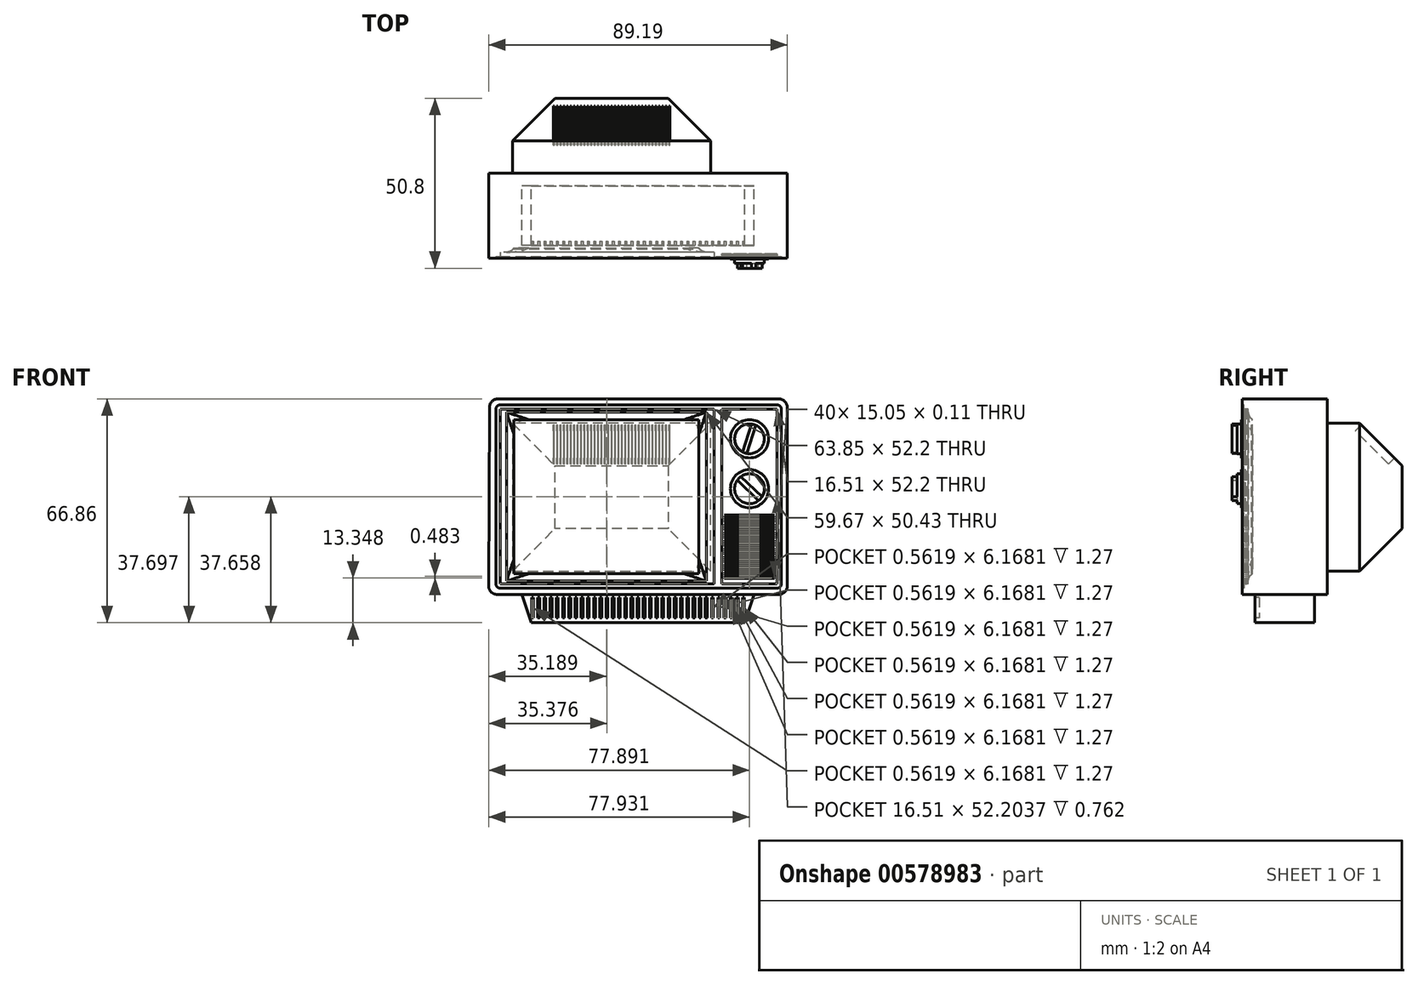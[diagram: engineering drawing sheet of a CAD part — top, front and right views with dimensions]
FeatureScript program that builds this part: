
annotation { "Feature Type Name" : "Feature", "Feature Type Description" : "" }
export const myFeature = defineFeature(function(context is Context, id is Id, definition is map)
    precondition{}
    {
        {
            var Q0;
            Q0=qCreatedBy(makeId("Front.planeOp"),FACE);
            var sketch = newSketch(context, id + "F0", { "sketchPlane" : qUnion([Q0])});
            skLineSegment(sketch, "E0", {"start": v(-47.46, 45.8) * mm, "end": v(41.44, 45.8) * mm});
            skLineSegment(sketch, "E1", {"start": v(41.44, 45.8) * mm, "end": v(41.44, -12.62) * mm});
            skLineSegment(sketch, "E2", {"start": v(41.44, -12.62) * mm, "end": v(-47.76, -12.62) * mm});
            skLineSegment(sketch, "E3", {"start": v(-47.76, -12.62) * mm, "end": v(-47.46, 45.8) * mm});
            skLineSegment(sketch, "E4", {"start": v(-35.06, -12.62) * mm, "end": v(-35.06, -21.06) * mm});
            skLineSegment(sketch, "E5", {"start": v(-35.06, -21.06) * mm, "end": v(28.74, -21.06) * mm});
            skLineSegment(sketch, "E6", {"start": v(28.74, -21.06) * mm, "end": v(28.74, -12.62) * mm});
            skLineSegment(sketch, "E7", {"start": v(-35.06, -21.06) * mm, "end": v(-37.87, -12.62) * mm});
            skLineSegment(sketch, "E8", {"start": v(28.74, -21.06) * mm, "end": v(31.55, -12.62) * mm});
            skSolve(sketch);
        }
        {
            var Q0;
            Q0=makeQuery(id+"F0.imprint","IMPRINT",FACE,{"disambiguationData":[TD([[makeQuery(id+"F0.imprint","IMPRINT",EDGE,{"derivedFrom":sQuery(id+"F0.wireOp",EDGE,"E0")}),-1.0]])]});
            extrude(context, id + "F1", {"entities" : qUnion([Q0]), "endBound" : BoundingType.SYMMETRIC, "depth" : 25.4 * mm, "offsetDistance" : 25.4 * mm});
        }
        {
            var Q0;
            {var subQ0=sQuery(id+"F0.wireOp",EDGE,"E4");Q0=makeQuery(id+"F0.imprint","IMPRINT",FACE,{"disambiguationData":[TD([[makeQuery(id+"F0.imprint","IMPRINT",EDGE,{"derivedFrom":subQ0}),1.0]])]});}
            var Q1;
            {var subQ0=sQuery(id+"F0.wireOp",EDGE,"E4");Q1=makeQuery(id+"F0.imprint","IMPRINT",FACE,{"disambiguationData":[TD([[makeQuery(id+"F0.imprint","IMPRINT",EDGE,{"derivedFrom":subQ0}),-1.0]])]});}
            var Q2;
            {var subQ0=sQuery(id+"F0.wireOp",EDGE,"E6");Q2=makeQuery(id+"F0.imprint","IMPRINT",FACE,{"disambiguationData":[TD([[makeQuery(id+"F0.imprint","IMPRINT",EDGE,{"derivedFrom":subQ0}),-1.0]])]});}
            extrude(context, id + "F2", {"entities" : qUnion([Q0, Q1, Q2]), "endBound" : BoundingType.SYMMETRIC, "depth" : 17.78 * mm, "offsetDistance" : 25.4 * mm});
        }
        {
            var Q0;
            Q0=makeQuery(id+"F1.opExtrude","CAP_FACE",FACE,{"disambiguationData":[OSD([sQuery(id+"F0.wireOp",EDGE,"E0"),sQuery(id+"F0.wireOp",EDGE,"E1"),sQuery(id+"F0.wireOp",EDGE,"E2"),sQuery(id+"F0.wireOp",EDGE,"E3")])],"isStart":false});
            var sketch = newSketch(context, id + "F3", { "sketchPlane" : qUnion([Q0])});
            skLineSegment(sketch, "E9", {"start": v(39.7, -10.73) * mm, "end": v(39.7, 44) * mm});
            skLineSegment(sketch, "E10", {"start": v(39.7, 44) * mm, "end": v(-45.57, 44) * mm});
            skLineSegment(sketch, "E11", {"start": v(-45.57, 44) * mm, "end": v(-45.57, -10.73) * mm});
            skLineSegment(sketch, "E12", {"start": v(-45.57, -10.73) * mm, "end": v(39.7, -10.73) * mm});
            skSolve(sketch);
        }
        {
            var Q0;
            Q0=makeQuery(id+"F1.opExtrude","SWEPT_EDGE",EDGE,{"disambiguationData":[OSD([sQuery(id+"F0.wireOp",EDGE,"E2"),sQuery(id+"F0.wireOp",EDGE,"E3")])]});
            var Q1;
            Q1=makeQuery(id+"F1.opExtrude","SWEPT_EDGE",EDGE,{"disambiguationData":[OSD([sQuery(id+"F0.wireOp",EDGE,"E1"),sQuery(id+"F0.wireOp",EDGE,"E2")])]});
            var Q2;
            Q2=makeQuery(id+"F1.opExtrude","SWEPT_EDGE",EDGE,{"disambiguationData":[OSD([sQuery(id+"F0.wireOp",EDGE,"E0"),sQuery(id+"F0.wireOp",EDGE,"E1")])]});
            var Q3;
            Q3=makeQuery(id+"F1.opExtrude","SWEPT_EDGE",EDGE,{"disambiguationData":[OSD([sQuery(id+"F0.wireOp",EDGE,"E0"),sQuery(id+"F0.wireOp",EDGE,"E3")])]});
            fillet(context, id + "F4", {"entities" : qUnion([Q0, Q1, Q2, Q3]), "radius" : 2.54 * mm, "tangentPropagation" : true, "allowEdgeOverflow" : false});
        }
        {
            var Q0;
            Q0 = qSketchRegion(id + "F3", true);
            extrude(context, id + "F5", {"entities" : qUnion([Q0]), "operationType" : NewBodyOperationType.REMOVE, "oppositeDirection" : true, "depth" : 0.5 * mm, "offsetDistance" : 25.4 * mm});
        }
        {
            var Q0;
            Q0=makeQuery(id+"F5.boolean.opBoolean","COPY",EDGE,{"derivedFrom":makeQuery(id+"F5.opExtrude","SWEPT_EDGE",EDGE,{"disambiguationData":[OSD([sQuery(id+"F3.wireOp",EDGE,"E10"),sQuery(id+"F3.wireOp",EDGE,"E11")])]})});
            var Q1;
            Q1=makeQuery(id+"F5.boolean.opBoolean","COPY",EDGE,{"derivedFrom":makeQuery(id+"F5.opExtrude","SWEPT_EDGE",EDGE,{"disambiguationData":[OSD([sQuery(id+"F3.wireOp",EDGE,"E9"),sQuery(id+"F3.wireOp",EDGE,"E10")])]})});
            var Q2;
            Q2=makeQuery(id+"F5.boolean.opBoolean","COPY",EDGE,{"derivedFrom":makeQuery(id+"F5.opExtrude","SWEPT_EDGE",EDGE,{"disambiguationData":[OSD([sQuery(id+"F3.wireOp",EDGE,"E9"),sQuery(id+"F3.wireOp",EDGE,"E12")])]})});
            var Q3;
            Q3=makeQuery(id+"F5.boolean.opBoolean","COPY",EDGE,{"derivedFrom":makeQuery(id+"F5.opExtrude","SWEPT_EDGE",EDGE,{"disambiguationData":[OSD([sQuery(id+"F3.wireOp",EDGE,"E11"),sQuery(id+"F3.wireOp",EDGE,"E12")])]})});
            fillet(context, id + "F6", {"entities" : qUnion([Q0, Q1, Q2, Q3]), "radius" : 1.27 * mm, "tangentPropagation" : true, "allowEdgeOverflow" : false});
        }
        {
            var Q0;
            Q0=makeQuery(id+"F1.opExtrude","CAP_FACE",FACE,{"disambiguationData":[OSD([sQuery(id+"F0.wireOp",EDGE,"E0"),sQuery(id+"F0.wireOp",EDGE,"E1"),sQuery(id+"F0.wireOp",EDGE,"E2"),sQuery(id+"F0.wireOp",EDGE,"E3")])],"isStart":true});
            var sketch = newSketch(context, id + "F7", { "sketchPlane" : qUnion([Q0])});
            skSolve(sketch);
        }
        {
            var Q0;
            Q0=makeQuery(id+"F5.boolean.opBoolean","COPY",FACE,{"derivedFrom":makeQuery(id+"F5.opExtrude","CAP_FACE",FACE,{"disambiguationData":[OSD([sQuery(id+"F3.wireOp",EDGE,"E9"),sQuery(id+"F3.wireOp",EDGE,"E10"),sQuery(id+"F3.wireOp",EDGE,"E11"),sQuery(id+"F3.wireOp",EDGE,"E12")])],"isStart":false})});
            var sketch = newSketch(context, id + "F8", { "sketchPlane" : qUnion([Q0])});
            skLineSegment(sketch, "E13", {"start": v(38.44, 42.74) * mm, "end": v(38.44, -9.46) * mm});
            skLineSegment(sketch, "E14", {"start": v(38.44, -9.46) * mm, "end": v(21.93, -9.46) * mm});
            skLineSegment(sketch, "E15", {"start": v(21.93, -9.46) * mm, "end": v(21.93, 42.74) * mm});
            skLineSegment(sketch, "E16", {"start": v(21.93, 42.74) * mm, "end": v(38.44, 42.74) * mm});
            skLineSegment(sketch, "E17", {"start": v(19.55, 42.74) * mm, "end": v(-44.3, 42.74) * mm});
            skLineSegment(sketch, "E18", {"start": v(-44.3, 42.74) * mm, "end": v(-44.3, -9.46) * mm});
            skLineSegment(sketch, "E19", {"start": v(-44.3, -9.46) * mm, "end": v(19.55, -9.46) * mm});
            skLineSegment(sketch, "E20", {"start": v(19.55, -9.46) * mm, "end": v(19.55, 42.74) * mm});
            skSolve(sketch);
        }
        {
            var Q0;
            {var subQ3=sQuery(id+"F0.wireOp",EDGE,"E0");Q0=makeQuery(id+"F7.imprint","IMPRINT",FACE,{"disambiguationData":[TD([[makeQuery(id+"F7.imprint","IMPRINT",EDGE,{"derivedFrom":makeQuery(id+"F1.opExtrude","CAP_EDGE",EDGE,{"disambiguationData":[OSD([subQ3])],"isStart":true})}),1.0]])]});}
            var sketch = newSketch(context, id + "F9", { "sketchPlane" : qUnion([Q0])});
            skLineSegment(sketch, "E21.bottom", {"start": v(-18.58, 38.52) * mm, "end": v(40.61, 38.52) * mm});
            skLineSegment(sketch, "E21.top", {"start": v(-18.58, -5.65) * mm, "end": v(40.61, -5.65) * mm});
            skLineSegment(sketch, "E21.left", {"start": v(-18.58, 38.52) * mm, "end": v(-18.58, -5.65) * mm});
            skLineSegment(sketch, "E21.right", {"start": v(40.61, 38.52) * mm, "end": v(40.61, -5.65) * mm});
            skSolve(sketch);
        }
        {
            var Q0;
            Q0 = qSketchRegion(id + "F9", true);
            extrude(context, id + "F10", {"entities" : qUnion([Q0]), "depth" : 22.35 * mm, "offsetDistance" : 25.4 * mm});
        }
        {
            var Q0;
            Q0=makeQuery(id+"F10.opExtrude","CAP_EDGE",EDGE,{"disambiguationData":[OSD([sQuery(id+"F9.wireOp",EDGE,"E21.left")])],"isStart":false});
            var Q1;
            Q1=makeQuery(id+"F10.opExtrude","CAP_EDGE",EDGE,{"disambiguationData":[OSD([sQuery(id+"F9.wireOp",EDGE,"E21.bottom")])],"isStart":false});
            var Q2;
            Q2=makeQuery(id+"F10.opExtrude","CAP_EDGE",EDGE,{"disambiguationData":[OSD([sQuery(id+"F9.wireOp",EDGE,"E21.right")])],"isStart":false});
            var Q3;
            Q3=makeQuery(id+"F10.opExtrude","CAP_EDGE",EDGE,{"disambiguationData":[OSD([sQuery(id+"F9.wireOp",EDGE,"E21.top")])],"isStart":false});
            chamfer(context, id + "F11", {"entities" : qUnion([Q0, Q1, Q2, Q3]), "width" : 12.7 * mm, "tangentPropagation" : true});
        }
        {
            var Q0;
            Q0=makeQuery(id+"F8.imprint","IMPRINT",FACE,{"disambiguationData":[TD([[makeQuery(id+"F8.imprint","IMPRINT",EDGE,{"derivedFrom":sQuery(id+"F8.wireOp",EDGE,"E17")}),1.0]])]});
            var sketch = newSketch(context, id + "F12", { "sketchPlane" : qUnion([Q0])});
            skLineSegment(sketch, "E22", {"start": v(-40.2, 39.61) * mm, "end": v(15.07, 39.61) * mm});
            skLineSegment(sketch, "E23", {"start": v(15.07, 39.61) * mm, "end": v(15.07, -6.42) * mm});
            skLineSegment(sketch, "E24", {"start": v(15.07, -6.42) * mm, "end": v(-40.2, -6.42) * mm});
            skLineSegment(sketch, "E25", {"start": v(-40.2, -6.42) * mm, "end": v(-40.2, 39.61) * mm});
            skSolve(sketch);
        }
        {
            var Q0;
            Q0=makeQuery(id+"F12.imprint","IMPRINT",FACE,{"disambiguationData":[TD([[makeQuery(id+"F12.imprint","IMPRINT",EDGE,{"derivedFrom":sQuery(id+"F12.wireOp",EDGE,"E22")}),-1.0]])]});
            extrude(context, id + "F13", {"entities" : qUnion([Q0]), "operationType" : NewBodyOperationType.REMOVE, "oppositeDirection" : true, "depth" : 2.54 * mm, "offsetDistance" : 25.4 * mm});
        }
        {
            var Q0;
            Q0=makeQuery(id+"F8.imprint","IMPRINT",FACE,{"disambiguationData":[TD([[makeQuery(id+"F8.imprint","IMPRINT",EDGE,{"derivedFrom":sQuery(id+"F8.wireOp",EDGE,"E17")}),1.0]])]});
            extrude(context, id + "F14", {"entities" : qUnion([Q0]), "operationType" : NewBodyOperationType.REMOVE, "oppositeDirection" : true, "depth" : 1.27 * mm, "offsetDistance" : 25.4 * mm});
        }
        {
            var Q0;
            Q0=makeQuery(id+"F14.boolean.opBoolean","INTERSECT",EDGE,{"derivedFrom":[makeQuery(id+"F13.boolean.opBoolean","COPY",FACE,{"derivedFrom":makeQuery(id+"F13.opExtrude","SWEPT_FACE",FACE,{"disambiguationData":[OSD([sQuery(id+"F12.wireOp",EDGE,"E25")])]})}),makeQuery(id+"F14.opExtrude","CAP_FACE",FACE,{"disambiguationData":[OSD([sQuery(id+"F8.wireOp",EDGE,"E17"),sQuery(id+"F8.wireOp",EDGE,"E18"),sQuery(id+"F8.wireOp",EDGE,"E19"),sQuery(id+"F8.wireOp",EDGE,"E20")])],"isStart":false})]});
            var Q1;
            Q1=makeQuery(id+"F14.boolean.opBoolean","INTERSECT",EDGE,{"derivedFrom":[makeQuery(id+"F13.boolean.opBoolean","COPY",FACE,{"derivedFrom":makeQuery(id+"F13.opExtrude","SWEPT_FACE",FACE,{"disambiguationData":[OSD([sQuery(id+"F12.wireOp",EDGE,"E22")])]})}),makeQuery(id+"F14.opExtrude","CAP_FACE",FACE,{"disambiguationData":[OSD([sQuery(id+"F8.wireOp",EDGE,"E17"),sQuery(id+"F8.wireOp",EDGE,"E18"),sQuery(id+"F8.wireOp",EDGE,"E19"),sQuery(id+"F8.wireOp",EDGE,"E20")])],"isStart":false})]});
            var Q2;
            Q2=makeQuery(id+"F14.boolean.opBoolean","INTERSECT",EDGE,{"derivedFrom":[makeQuery(id+"F13.boolean.opBoolean","COPY",FACE,{"derivedFrom":makeQuery(id+"F13.opExtrude","SWEPT_FACE",FACE,{"disambiguationData":[OSD([sQuery(id+"F12.wireOp",EDGE,"E23")])]})}),makeQuery(id+"F14.opExtrude","CAP_FACE",FACE,{"disambiguationData":[OSD([sQuery(id+"F8.wireOp",EDGE,"E17"),sQuery(id+"F8.wireOp",EDGE,"E18"),sQuery(id+"F8.wireOp",EDGE,"E19"),sQuery(id+"F8.wireOp",EDGE,"E20")])],"isStart":false})]});
            var Q3;
            Q3=makeQuery(id+"F14.boolean.opBoolean","INTERSECT",EDGE,{"derivedFrom":[makeQuery(id+"F13.boolean.opBoolean","COPY",FACE,{"derivedFrom":makeQuery(id+"F13.opExtrude","SWEPT_FACE",FACE,{"disambiguationData":[OSD([sQuery(id+"F12.wireOp",EDGE,"E24")])]})}),makeQuery(id+"F14.opExtrude","CAP_FACE",FACE,{"disambiguationData":[OSD([sQuery(id+"F8.wireOp",EDGE,"E17"),sQuery(id+"F8.wireOp",EDGE,"E18"),sQuery(id+"F8.wireOp",EDGE,"E19"),sQuery(id+"F8.wireOp",EDGE,"E20")])],"isStart":false})]});
            fillet(context, id + "F15", {"entities" : qUnion([Q0, Q1, Q2, Q3]), "radius" : 2.54 * mm, "tangentPropagation" : true, "allowEdgeOverflow" : false});
        }
        {
            var Q0;
            Q0=makeQuery(id+"F13.boolean.opBoolean","COPY",FACE,{"derivedFrom":makeQuery(id+"F13.opExtrude","CAP_FACE",FACE,{"disambiguationData":[OSD([sQuery(id+"F12.wireOp",EDGE,"E22"),sQuery(id+"F12.wireOp",EDGE,"E23"),sQuery(id+"F12.wireOp",EDGE,"E24"),sQuery(id+"F12.wireOp",EDGE,"E25")])],"isStart":false})});
            extrude(context, id + "F16", {"entities" : qUnion([Q0]), "depth" : 0.25 * mm, "offsetDistance" : 25.4 * mm});
        }
        {
            var Q0;
            Q0=makeQuery(id+"F14.boolean.opBoolean","COPY",FACE,{"derivedFrom":makeQuery(id+"F14.opExtrude","CAP_FACE",FACE,{"disambiguationData":[OSD([sQuery(id+"F8.wireOp",EDGE,"E17"),sQuery(id+"F8.wireOp",EDGE,"E18"),sQuery(id+"F8.wireOp",EDGE,"E19"),sQuery(id+"F8.wireOp",EDGE,"E20")])],"isStart":false})});
            extrude(context, id + "F17", {"entities" : qUnion([Q0]), "depth" : 0 * mm, "offsetDistance" : 25.4 * mm});
        }
        {
            var Q0;
            {var subQ0=makeQuery(id+"F14.opExtrude","CAP_FACE",FACE,{"disambiguationData":[OSD([sQuery(id+"F8.wireOp",EDGE,"E17"),sQuery(id+"F8.wireOp",EDGE,"E18"),sQuery(id+"F8.wireOp",EDGE,"E19"),sQuery(id+"F8.wireOp",EDGE,"E20")])],"isStart":false});Q0=makeQuery(id+"F15.opFillet","BLEND_EDGE",EDGE,{"blendedFrom":[makeQuery(id+"F14.boolean.opBoolean","INTERSECT",EDGE,{"derivedFrom":[makeQuery(id+"F13.boolean.opBoolean","COPY",FACE,{"derivedFrom":makeQuery(id+"F13.opExtrude","SWEPT_FACE",FACE,{"disambiguationData":[OSD([sQuery(id+"F12.wireOp",EDGE,"E22")])]})}),subQ0]}),makeQuery(id+"F14.boolean.opBoolean","INTERSECT",EDGE,{"derivedFrom":[makeQuery(id+"F13.boolean.opBoolean","COPY",FACE,{"derivedFrom":makeQuery(id+"F13.opExtrude","SWEPT_FACE",FACE,{"disambiguationData":[OSD([sQuery(id+"F12.wireOp",EDGE,"E25")])]})}),subQ0]})],"blendedInto":[]});}
            var Q1;
            {var subQ0=makeQuery(id+"F14.opExtrude","CAP_FACE",FACE,{"disambiguationData":[OSD([sQuery(id+"F8.wireOp",EDGE,"E17"),sQuery(id+"F8.wireOp",EDGE,"E18"),sQuery(id+"F8.wireOp",EDGE,"E19"),sQuery(id+"F8.wireOp",EDGE,"E20")])],"isStart":false});Q1=makeQuery(id+"F15.opFillet","BLEND_EDGE",EDGE,{"blendedFrom":[makeQuery(id+"F14.boolean.opBoolean","INTERSECT",EDGE,{"derivedFrom":[makeQuery(id+"F13.boolean.opBoolean","COPY",FACE,{"derivedFrom":makeQuery(id+"F13.opExtrude","SWEPT_FACE",FACE,{"disambiguationData":[OSD([sQuery(id+"F12.wireOp",EDGE,"E24")])]})}),subQ0]}),makeQuery(id+"F14.boolean.opBoolean","INTERSECT",EDGE,{"derivedFrom":[makeQuery(id+"F13.boolean.opBoolean","COPY",FACE,{"derivedFrom":makeQuery(id+"F13.opExtrude","SWEPT_FACE",FACE,{"disambiguationData":[OSD([sQuery(id+"F12.wireOp",EDGE,"E25")])]})}),subQ0]})],"blendedInto":[]});}
            var Q2;
            {var subQ0=makeQuery(id+"F14.opExtrude","CAP_FACE",FACE,{"disambiguationData":[OSD([sQuery(id+"F8.wireOp",EDGE,"E17"),sQuery(id+"F8.wireOp",EDGE,"E18"),sQuery(id+"F8.wireOp",EDGE,"E19"),sQuery(id+"F8.wireOp",EDGE,"E20")])],"isStart":false});Q2=makeQuery(id+"F15.opFillet","BLEND_EDGE",EDGE,{"blendedFrom":[makeQuery(id+"F14.boolean.opBoolean","INTERSECT",EDGE,{"derivedFrom":[makeQuery(id+"F13.boolean.opBoolean","COPY",FACE,{"derivedFrom":makeQuery(id+"F13.opExtrude","SWEPT_FACE",FACE,{"disambiguationData":[OSD([sQuery(id+"F12.wireOp",EDGE,"E23")])]})}),subQ0]}),makeQuery(id+"F14.boolean.opBoolean","INTERSECT",EDGE,{"derivedFrom":[makeQuery(id+"F13.boolean.opBoolean","COPY",FACE,{"derivedFrom":makeQuery(id+"F13.opExtrude","SWEPT_FACE",FACE,{"disambiguationData":[OSD([sQuery(id+"F12.wireOp",EDGE,"E24")])]})}),subQ0]})],"blendedInto":[]});}
            var Q3;
            {var subQ0=makeQuery(id+"F14.opExtrude","CAP_FACE",FACE,{"disambiguationData":[OSD([sQuery(id+"F8.wireOp",EDGE,"E17"),sQuery(id+"F8.wireOp",EDGE,"E18"),sQuery(id+"F8.wireOp",EDGE,"E19"),sQuery(id+"F8.wireOp",EDGE,"E20")])],"isStart":false});Q3=makeQuery(id+"F15.opFillet","BLEND_EDGE",EDGE,{"blendedFrom":[makeQuery(id+"F14.boolean.opBoolean","INTERSECT",EDGE,{"derivedFrom":[makeQuery(id+"F13.boolean.opBoolean","COPY",FACE,{"derivedFrom":makeQuery(id+"F13.opExtrude","SWEPT_FACE",FACE,{"disambiguationData":[OSD([sQuery(id+"F12.wireOp",EDGE,"E22")])]})}),subQ0]}),makeQuery(id+"F14.boolean.opBoolean","INTERSECT",EDGE,{"derivedFrom":[makeQuery(id+"F13.boolean.opBoolean","COPY",FACE,{"derivedFrom":makeQuery(id+"F13.opExtrude","SWEPT_FACE",FACE,{"disambiguationData":[OSD([sQuery(id+"F12.wireOp",EDGE,"E23")])]})}),subQ0]})],"blendedInto":[]});}
            fillet(context, id + "F18", {"entities" : qUnion([Q0, Q1, Q2, Q3]), "radius" : 5.08 * mm, "tangentPropagation" : true, "allowEdgeOverflow" : false});
        }
        {
            var Q0;
            Q0=makeQuery(id+"F2.opExtrude","CAP_FACE",FACE,{"disambiguationData":[OSD([sQuery(id+"F0.wireOp",EDGE,"E2"),sQuery(id+"F0.wireOp",EDGE,"E5"),sQuery(id+"F0.wireOp",EDGE,"E7"),sQuery(id+"F0.wireOp",EDGE,"E8")])],"isStart":false});
            var sketch = newSketch(context, id + "F19", { "sketchPlane" : qUnion([Q0])});
            skLineSegment(sketch, "E26.bottom", {"start": v(-34.94, -13.47) * mm, "end": v(-34.38, -13.47) * mm});
            skLineSegment(sketch, "E26.top", {"start": v(-34.94, -19.64) * mm, "end": v(-34.38, -19.64) * mm});
            skLineSegment(sketch, "E26.left", {"start": v(-34.94, -13.47) * mm, "end": v(-34.94, -19.64) * mm});
            skLineSegment(sketch, "E26.right", {"start": v(-34.38, -13.47) * mm, "end": v(-34.38, -19.64) * mm});
            skLineSegment(sketch, "E27.1.0.0", {"start": v(-33.1, -13.47) * mm, "end": v(-33.1, -19.64) * mm});
            skLineSegment(sketch, "E27.1.0.1", {"start": v(-32.53, -13.47) * mm, "end": v(-32.53, -19.64) * mm});
            skLineSegment(sketch, "E27.1.0.2", {"start": v(-33.1, -19.64) * mm, "end": v(-32.53, -19.64) * mm});
            skLineSegment(sketch, "E27.1.0.3", {"start": v(-33.1, -13.47) * mm, "end": v(-32.53, -13.47) * mm});
            skLineSegment(sketch, "E27.2.0.0", {"start": v(-31.24, -13.47) * mm, "end": v(-31.24, -19.64) * mm});
            skLineSegment(sketch, "E27.2.0.1", {"start": v(-30.67, -13.47) * mm, "end": v(-30.67, -19.64) * mm});
            skLineSegment(sketch, "E27.2.0.2", {"start": v(-31.24, -19.64) * mm, "end": v(-30.67, -19.64) * mm});
            skLineSegment(sketch, "E27.2.0.3", {"start": v(-31.24, -13.47) * mm, "end": v(-30.67, -13.47) * mm});
            skLineSegment(sketch, "E27.3.0.0", {"start": v(-29.38, -13.47) * mm, "end": v(-29.38, -19.64) * mm});
            skLineSegment(sketch, "E27.3.0.1", {"start": v(-28.82, -13.47) * mm, "end": v(-28.82, -19.64) * mm});
            skLineSegment(sketch, "E27.3.0.2", {"start": v(-29.38, -19.64) * mm, "end": v(-28.82, -19.64) * mm});
            skLineSegment(sketch, "E27.3.0.3", {"start": v(-29.38, -13.47) * mm, "end": v(-28.82, -13.47) * mm});
            skLineSegment(sketch, "E27.4.0.0", {"start": v(-27.53, -13.47) * mm, "end": v(-27.53, -19.64) * mm});
            skLineSegment(sketch, "E27.4.0.1", {"start": v(-26.97, -13.47) * mm, "end": v(-26.97, -19.64) * mm});
            skLineSegment(sketch, "E27.4.0.2", {"start": v(-27.53, -19.64) * mm, "end": v(-26.97, -19.64) * mm});
            skLineSegment(sketch, "E27.4.0.3", {"start": v(-27.53, -13.47) * mm, "end": v(-26.97, -13.47) * mm});
            skLineSegment(sketch, "E27.5.0.0", {"start": v(-25.67, -13.47) * mm, "end": v(-25.67, -19.64) * mm});
            skLineSegment(sketch, "E27.5.0.1", {"start": v(-25.11, -13.47) * mm, "end": v(-25.11, -19.64) * mm});
            skLineSegment(sketch, "E27.5.0.2", {"start": v(-25.67, -19.64) * mm, "end": v(-25.11, -19.64) * mm});
            skLineSegment(sketch, "E27.5.0.3", {"start": v(-25.67, -13.47) * mm, "end": v(-25.11, -13.47) * mm});
            skLineSegment(sketch, "E27.6.0.0", {"start": v(-23.82, -13.47) * mm, "end": v(-23.82, -19.64) * mm});
            skLineSegment(sketch, "E27.6.0.1", {"start": v(-23.26, -13.47) * mm, "end": v(-23.26, -19.64) * mm});
            skLineSegment(sketch, "E27.6.0.2", {"start": v(-23.82, -19.64) * mm, "end": v(-23.26, -19.64) * mm});
            skLineSegment(sketch, "E27.6.0.3", {"start": v(-23.82, -13.47) * mm, "end": v(-23.26, -13.47) * mm});
            skLineSegment(sketch, "E27.7.0.0", {"start": v(-21.97, -13.47) * mm, "end": v(-21.97, -19.64) * mm});
            skLineSegment(sketch, "E27.7.0.1", {"start": v(-21.4, -13.47) * mm, "end": v(-21.4, -19.64) * mm});
            skLineSegment(sketch, "E27.7.0.2", {"start": v(-21.97, -19.64) * mm, "end": v(-21.4, -19.64) * mm});
            skLineSegment(sketch, "E27.7.0.3", {"start": v(-21.97, -13.47) * mm, "end": v(-21.4, -13.47) * mm});
            skLineSegment(sketch, "E27.8.0.0", {"start": v(-20.11, -13.47) * mm, "end": v(-20.11, -19.64) * mm});
            skLineSegment(sketch, "E27.8.0.1", {"start": v(-19.55, -13.47) * mm, "end": v(-19.55, -19.64) * mm});
            skLineSegment(sketch, "E27.8.0.2", {"start": v(-20.11, -19.64) * mm, "end": v(-19.55, -19.64) * mm});
            skLineSegment(sketch, "E27.8.0.3", {"start": v(-20.11, -13.47) * mm, "end": v(-19.55, -13.47) * mm});
            skLineSegment(sketch, "E27.9.0.0", {"start": v(-18.26, -13.47) * mm, "end": v(-18.26, -19.64) * mm});
            skLineSegment(sketch, "E27.9.0.1", {"start": v(-17.7, -13.47) * mm, "end": v(-17.7, -19.64) * mm});
            skLineSegment(sketch, "E27.9.0.2", {"start": v(-18.26, -19.64) * mm, "end": v(-17.7, -19.64) * mm});
            skLineSegment(sketch, "E27.9.0.3", {"start": v(-18.26, -13.47) * mm, "end": v(-17.7, -13.47) * mm});
            skLineSegment(sketch, "E27.10.0.0", {"start": v(-16.4, -13.47) * mm, "end": v(-16.4, -19.64) * mm});
            skLineSegment(sketch, "E27.10.0.1", {"start": v(-15.84, -13.47) * mm, "end": v(-15.84, -19.64) * mm});
            skLineSegment(sketch, "E27.10.0.2", {"start": v(-16.4, -19.64) * mm, "end": v(-15.84, -19.64) * mm});
            skLineSegment(sketch, "E27.10.0.3", {"start": v(-16.4, -13.47) * mm, "end": v(-15.84, -13.47) * mm});
            skLineSegment(sketch, "E27.11.0.0", {"start": v(-14.55, -13.47) * mm, "end": v(-14.55, -19.64) * mm});
            skLineSegment(sketch, "E27.11.0.1", {"start": v(-13.99, -13.47) * mm, "end": v(-13.99, -19.64) * mm});
            skLineSegment(sketch, "E27.11.0.2", {"start": v(-14.55, -19.64) * mm, "end": v(-13.99, -19.64) * mm});
            skLineSegment(sketch, "E27.11.0.3", {"start": v(-14.55, -13.47) * mm, "end": v(-13.99, -13.47) * mm});
            skLineSegment(sketch, "E27.12.0.0", {"start": v(-12.7, -13.47) * mm, "end": v(-12.7, -19.64) * mm});
            skLineSegment(sketch, "E27.12.0.1", {"start": v(-12.13, -13.47) * mm, "end": v(-12.13, -19.64) * mm});
            skLineSegment(sketch, "E27.12.0.2", {"start": v(-12.7, -19.64) * mm, "end": v(-12.13, -19.64) * mm});
            skLineSegment(sketch, "E27.12.0.3", {"start": v(-12.7, -13.47) * mm, "end": v(-12.13, -13.47) * mm});
            skLineSegment(sketch, "E27.13.0.0", {"start": v(-10.84, -13.47) * mm, "end": v(-10.84, -19.64) * mm});
            skLineSegment(sketch, "E27.13.0.1", {"start": v(-10.28, -13.47) * mm, "end": v(-10.28, -19.64) * mm});
            skLineSegment(sketch, "E27.13.0.2", {"start": v(-10.84, -19.64) * mm, "end": v(-10.28, -19.64) * mm});
            skLineSegment(sketch, "E27.13.0.3", {"start": v(-10.84, -13.47) * mm, "end": v(-10.28, -13.47) * mm});
            skLineSegment(sketch, "E27.14.0.0", {"start": v(-8.99, -13.47) * mm, "end": v(-8.99, -19.64) * mm});
            skLineSegment(sketch, "E27.14.0.1", {"start": v(-8.42, -13.47) * mm, "end": v(-8.42, -19.64) * mm});
            skLineSegment(sketch, "E27.14.0.2", {"start": v(-8.99, -19.64) * mm, "end": v(-8.42, -19.64) * mm});
            skLineSegment(sketch, "E27.14.0.3", {"start": v(-8.99, -13.47) * mm, "end": v(-8.42, -13.47) * mm});
            skLineSegment(sketch, "E27.15.0.0", {"start": v(-7.13, -13.47) * mm, "end": v(-7.13, -19.64) * mm});
            skLineSegment(sketch, "E27.15.0.1", {"start": v(-6.57, -13.47) * mm, "end": v(-6.57, -19.64) * mm});
            skLineSegment(sketch, "E27.15.0.2", {"start": v(-7.13, -19.64) * mm, "end": v(-6.57, -19.64) * mm});
            skLineSegment(sketch, "E27.15.0.3", {"start": v(-7.13, -13.47) * mm, "end": v(-6.57, -13.47) * mm});
            skLineSegment(sketch, "E27.16.0.0", {"start": v(-5.28, -13.47) * mm, "end": v(-5.28, -19.64) * mm});
            skLineSegment(sketch, "E27.16.0.1", {"start": v(-4.72, -13.47) * mm, "end": v(-4.72, -19.64) * mm});
            skLineSegment(sketch, "E27.16.0.2", {"start": v(-5.28, -19.64) * mm, "end": v(-4.72, -19.64) * mm});
            skLineSegment(sketch, "E27.16.0.3", {"start": v(-5.28, -13.47) * mm, "end": v(-4.72, -13.47) * mm});
            skLineSegment(sketch, "E27.17.0.0", {"start": v(-3.42, -13.47) * mm, "end": v(-3.42, -19.64) * mm});
            skLineSegment(sketch, "E27.17.0.1", {"start": v(-2.86, -13.47) * mm, "end": v(-2.86, -19.64) * mm});
            skLineSegment(sketch, "E27.17.0.2", {"start": v(-3.42, -19.64) * mm, "end": v(-2.86, -19.64) * mm});
            skLineSegment(sketch, "E27.17.0.3", {"start": v(-3.42, -13.47) * mm, "end": v(-2.86, -13.47) * mm});
            skLineSegment(sketch, "E27.18.0.0", {"start": v(-1.57, -13.47) * mm, "end": v(-1.57, -19.64) * mm});
            skLineSegment(sketch, "E27.18.0.1", {"start": v(-1, -13.47) * mm, "end": v(-1, -19.64) * mm});
            skLineSegment(sketch, "E27.18.0.2", {"start": v(-1.57, -19.64) * mm, "end": v(-1, -19.64) * mm});
            skLineSegment(sketch, "E27.18.0.3", {"start": v(-1.57, -13.47) * mm, "end": v(-1, -13.47) * mm});
            skLineSegment(sketch, "E27.19.0.0", {"start": v(0.29, -13.47) * mm, "end": v(0.29, -19.64) * mm});
            skLineSegment(sketch, "E27.19.0.1", {"start": v(0.85, -13.47) * mm, "end": v(0.85, -19.64) * mm});
            skLineSegment(sketch, "E27.19.0.2", {"start": v(0.29, -19.64) * mm, "end": v(0.85, -19.64) * mm});
            skLineSegment(sketch, "E27.19.0.3", {"start": v(0.29, -13.47) * mm, "end": v(0.85, -13.47) * mm});
            skLineSegment(sketch, "E27.20.0.0", {"start": v(2.14, -13.47) * mm, "end": v(2.14, -19.64) * mm});
            skLineSegment(sketch, "E27.20.0.1", {"start": v(2.7, -13.47) * mm, "end": v(2.7, -19.64) * mm});
            skLineSegment(sketch, "E27.20.0.2", {"start": v(2.14, -19.64) * mm, "end": v(2.7, -19.64) * mm});
            skLineSegment(sketch, "E27.20.0.3", {"start": v(2.14, -13.47) * mm, "end": v(2.7, -13.47) * mm});
            skLineSegment(sketch, "E27.21.0.0", {"start": v(4, -13.47) * mm, "end": v(4, -19.64) * mm});
            skLineSegment(sketch, "E27.21.0.1", {"start": v(4.56, -13.47) * mm, "end": v(4.56, -19.64) * mm});
            skLineSegment(sketch, "E27.21.0.2", {"start": v(4, -19.64) * mm, "end": v(4.56, -19.64) * mm});
            skLineSegment(sketch, "E27.21.0.3", {"start": v(4, -13.47) * mm, "end": v(4.56, -13.47) * mm});
            skLineSegment(sketch, "E27.22.0.0", {"start": v(5.85, -13.47) * mm, "end": v(5.85, -19.64) * mm});
            skLineSegment(sketch, "E27.22.0.1", {"start": v(6.4, -13.47) * mm, "end": v(6.4, -19.64) * mm});
            skLineSegment(sketch, "E27.22.0.2", {"start": v(5.85, -19.64) * mm, "end": v(6.4, -19.64) * mm});
            skLineSegment(sketch, "E27.22.0.3", {"start": v(5.85, -13.47) * mm, "end": v(6.4, -13.47) * mm});
            skLineSegment(sketch, "E27.23.0.0", {"start": v(7.7, -13.47) * mm, "end": v(7.7, -19.64) * mm});
            skLineSegment(sketch, "E27.23.0.1", {"start": v(8.26, -13.47) * mm, "end": v(8.26, -19.64) * mm});
            skLineSegment(sketch, "E27.23.0.2", {"start": v(7.7, -19.64) * mm, "end": v(8.26, -19.64) * mm});
            skLineSegment(sketch, "E27.23.0.3", {"start": v(7.7, -13.47) * mm, "end": v(8.26, -13.47) * mm});
            skLineSegment(sketch, "E27.24.0.0", {"start": v(9.56, -13.47) * mm, "end": v(9.56, -19.64) * mm});
            skLineSegment(sketch, "E27.24.0.1", {"start": v(10.12, -13.47) * mm, "end": v(10.12, -19.64) * mm});
            skLineSegment(sketch, "E27.24.0.2", {"start": v(9.56, -19.64) * mm, "end": v(10.12, -19.64) * mm});
            skLineSegment(sketch, "E27.24.0.3", {"start": v(9.56, -13.47) * mm, "end": v(10.12, -13.47) * mm});
            skLineSegment(sketch, "E27.25.0.0", {"start": v(11.41, -13.47) * mm, "end": v(11.41, -19.64) * mm});
            skLineSegment(sketch, "E27.25.0.1", {"start": v(11.97, -13.47) * mm, "end": v(11.97, -19.64) * mm});
            skLineSegment(sketch, "E27.25.0.2", {"start": v(11.41, -19.64) * mm, "end": v(11.97, -19.64) * mm});
            skLineSegment(sketch, "E27.25.0.3", {"start": v(11.41, -13.47) * mm, "end": v(11.97, -13.47) * mm});
            skLineSegment(sketch, "E27.26.0.0", {"start": v(13.26, -13.47) * mm, "end": v(13.26, -19.64) * mm});
            skLineSegment(sketch, "E27.26.0.1", {"start": v(13.83, -13.47) * mm, "end": v(13.83, -19.64) * mm});
            skLineSegment(sketch, "E27.26.0.2", {"start": v(13.26, -19.64) * mm, "end": v(13.83, -19.64) * mm});
            skLineSegment(sketch, "E27.26.0.3", {"start": v(13.26, -13.47) * mm, "end": v(13.83, -13.47) * mm});
            skLineSegment(sketch, "E27.27.0.0", {"start": v(15.12, -13.47) * mm, "end": v(15.12, -19.64) * mm});
            skLineSegment(sketch, "E27.27.0.1", {"start": v(15.68, -13.47) * mm, "end": v(15.68, -19.64) * mm});
            skLineSegment(sketch, "E27.27.0.2", {"start": v(15.12, -19.64) * mm, "end": v(15.68, -19.64) * mm});
            skLineSegment(sketch, "E27.27.0.3", {"start": v(15.12, -13.47) * mm, "end": v(15.68, -13.47) * mm});
            skLineSegment(sketch, "E27.28.0.0", {"start": v(16.97, -13.47) * mm, "end": v(16.97, -19.64) * mm});
            skLineSegment(sketch, "E27.28.0.1", {"start": v(17.53, -13.47) * mm, "end": v(17.53, -19.64) * mm});
            skLineSegment(sketch, "E27.28.0.2", {"start": v(16.97, -19.64) * mm, "end": v(17.53, -19.64) * mm});
            skLineSegment(sketch, "E27.28.0.3", {"start": v(16.97, -13.47) * mm, "end": v(17.53, -13.47) * mm});
            skLineSegment(sketch, "E27.29.0.0", {"start": v(18.83, -13.47) * mm, "end": v(18.83, -19.64) * mm});
            skLineSegment(sketch, "E27.29.0.1", {"start": v(19.39, -13.47) * mm, "end": v(19.39, -19.64) * mm});
            skLineSegment(sketch, "E27.29.0.2", {"start": v(18.83, -19.64) * mm, "end": v(19.39, -19.64) * mm});
            skLineSegment(sketch, "E27.29.0.3", {"start": v(18.83, -13.47) * mm, "end": v(19.39, -13.47) * mm});
            skLineSegment(sketch, "E27.30.0.0", {"start": v(20.68, -13.47) * mm, "end": v(20.68, -19.64) * mm});
            skLineSegment(sketch, "E27.30.0.1", {"start": v(21.24, -13.47) * mm, "end": v(21.24, -19.64) * mm});
            skLineSegment(sketch, "E27.30.0.2", {"start": v(20.68, -19.64) * mm, "end": v(21.24, -19.64) * mm});
            skLineSegment(sketch, "E27.30.0.3", {"start": v(20.68, -13.47) * mm, "end": v(21.24, -13.47) * mm});
            skLineSegment(sketch, "E27.31.0.0", {"start": v(22.54, -13.47) * mm, "end": v(22.54, -19.64) * mm});
            skLineSegment(sketch, "E27.31.0.1", {"start": v(23.1, -13.47) * mm, "end": v(23.1, -19.64) * mm});
            skLineSegment(sketch, "E27.31.0.2", {"start": v(22.54, -19.64) * mm, "end": v(23.1, -19.64) * mm});
            skLineSegment(sketch, "E27.31.0.3", {"start": v(22.54, -13.47) * mm, "end": v(23.1, -13.47) * mm});
            skLineSegment(sketch, "E27.32.0.0", {"start": v(24.39, -13.47) * mm, "end": v(24.39, -19.64) * mm});
            skLineSegment(sketch, "E27.32.0.1", {"start": v(24.95, -13.47) * mm, "end": v(24.95, -19.64) * mm});
            skLineSegment(sketch, "E27.32.0.2", {"start": v(24.39, -19.64) * mm, "end": v(24.95, -19.64) * mm});
            skLineSegment(sketch, "E27.32.0.3", {"start": v(24.39, -13.47) * mm, "end": v(24.95, -13.47) * mm});
            skLineSegment(sketch, "E27.33.0.0", {"start": v(26.24, -13.47) * mm, "end": v(26.24, -19.64) * mm});
            skLineSegment(sketch, "E27.33.0.1", {"start": v(26.8, -13.47) * mm, "end": v(26.8, -19.64) * mm});
            skLineSegment(sketch, "E27.33.0.2", {"start": v(26.24, -19.64) * mm, "end": v(26.8, -19.64) * mm});
            skLineSegment(sketch, "E27.33.0.3", {"start": v(26.24, -13.47) * mm, "end": v(26.8, -13.47) * mm});
            skLineSegment(sketch, "E27.34.0.0", {"start": v(28.1, -13.47) * mm, "end": v(28.1, -19.64) * mm});
            skLineSegment(sketch, "E27.34.0.1", {"start": v(28.66, -13.47) * mm, "end": v(28.66, -19.64) * mm});
            skLineSegment(sketch, "E27.34.0.2", {"start": v(28.1, -19.64) * mm, "end": v(28.66, -19.64) * mm});
            skLineSegment(sketch, "E27.34.0.3", {"start": v(28.1, -13.47) * mm, "end": v(28.66, -13.47) * mm});
            skLineSegment(sketch, "E27.direction1", {"start": v(-34.94, -19.64) * mm, "end": v(-33.1, -19.64) * mm, "construction": true});
            skSolve(sketch);
        }
        {
            var Q0;
            Q0=makeQuery(id+"F19.imprint","IMPRINT",FACE,{"disambiguationData":[TD([[makeQuery(id+"F19.imprint","IMPRINT",EDGE,{"derivedFrom":sQuery(id+"F19.wireOp",EDGE,"E26.bottom")}),-1.0]])]});
            var Q1;
            Q1=makeQuery(id+"F19.imprint","IMPRINT",FACE,{"disambiguationData":[TD([[makeQuery(id+"F19.imprint","IMPRINT",EDGE,{"derivedFrom":sQuery(id+"F19.wireOp",EDGE,"E27.1.0.0")}),1.0]])]});
            var Q2;
            Q2=makeQuery(id+"F19.imprint","IMPRINT",FACE,{"disambiguationData":[TD([[makeQuery(id+"F19.imprint","IMPRINT",EDGE,{"derivedFrom":sQuery(id+"F19.wireOp",EDGE,"E27.2.0.0")}),1.0]])]});
            var Q3;
            Q3=makeQuery(id+"F19.imprint","IMPRINT",FACE,{"disambiguationData":[TD([[makeQuery(id+"F19.imprint","IMPRINT",EDGE,{"derivedFrom":sQuery(id+"F19.wireOp",EDGE,"E27.3.0.0")}),1.0]])]});
            var Q4;
            Q4=makeQuery(id+"F19.imprint","IMPRINT",FACE,{"disambiguationData":[TD([[makeQuery(id+"F19.imprint","IMPRINT",EDGE,{"derivedFrom":sQuery(id+"F19.wireOp",EDGE,"E27.4.0.0")}),1.0]])]});
            var Q5;
            Q5=makeQuery(id+"F19.imprint","IMPRINT",FACE,{"disambiguationData":[TD([[makeQuery(id+"F19.imprint","IMPRINT",EDGE,{"derivedFrom":sQuery(id+"F19.wireOp",EDGE,"E27.5.0.0")}),1.0]])]});
            var Q6;
            Q6=makeQuery(id+"F19.imprint","IMPRINT",FACE,{"disambiguationData":[TD([[makeQuery(id+"F19.imprint","IMPRINT",EDGE,{"derivedFrom":sQuery(id+"F19.wireOp",EDGE,"E27.6.0.0")}),1.0]])]});
            var Q7;
            Q7=makeQuery(id+"F19.imprint","IMPRINT",FACE,{"disambiguationData":[TD([[makeQuery(id+"F19.imprint","IMPRINT",EDGE,{"derivedFrom":sQuery(id+"F19.wireOp",EDGE,"E27.7.0.0")}),1.0]])]});
            var Q8;
            Q8=makeQuery(id+"F19.imprint","IMPRINT",FACE,{"disambiguationData":[TD([[makeQuery(id+"F19.imprint","IMPRINT",EDGE,{"derivedFrom":sQuery(id+"F19.wireOp",EDGE,"E27.9.0.0")}),1.0]])]});
            var Q9;
            Q9=makeQuery(id+"F19.imprint","IMPRINT",FACE,{"disambiguationData":[TD([[makeQuery(id+"F19.imprint","IMPRINT",EDGE,{"derivedFrom":sQuery(id+"F19.wireOp",EDGE,"E27.8.0.0")}),1.0]])]});
            var Q10;
            Q10=makeQuery(id+"F19.imprint","IMPRINT",FACE,{"disambiguationData":[TD([[makeQuery(id+"F19.imprint","IMPRINT",EDGE,{"derivedFrom":sQuery(id+"F19.wireOp",EDGE,"E27.10.0.0")}),1.0]])]});
            var Q11;
            Q11=makeQuery(id+"F19.imprint","IMPRINT",FACE,{"disambiguationData":[TD([[makeQuery(id+"F19.imprint","IMPRINT",EDGE,{"derivedFrom":sQuery(id+"F19.wireOp",EDGE,"E27.11.0.0")}),1.0]])]});
            var Q12;
            Q12=makeQuery(id+"F19.imprint","IMPRINT",FACE,{"disambiguationData":[TD([[makeQuery(id+"F19.imprint","IMPRINT",EDGE,{"derivedFrom":sQuery(id+"F19.wireOp",EDGE,"E27.12.0.0")}),1.0]])]});
            var Q13;
            Q13=makeQuery(id+"F19.imprint","IMPRINT",FACE,{"disambiguationData":[TD([[makeQuery(id+"F19.imprint","IMPRINT",EDGE,{"derivedFrom":sQuery(id+"F19.wireOp",EDGE,"E27.13.0.0")}),1.0]])]});
            var Q14;
            Q14=makeQuery(id+"F19.imprint","IMPRINT",FACE,{"disambiguationData":[TD([[makeQuery(id+"F19.imprint","IMPRINT",EDGE,{"derivedFrom":sQuery(id+"F19.wireOp",EDGE,"E27.14.0.0")}),1.0]])]});
            var Q15;
            Q15=makeQuery(id+"F19.imprint","IMPRINT",FACE,{"disambiguationData":[TD([[makeQuery(id+"F19.imprint","IMPRINT",EDGE,{"derivedFrom":sQuery(id+"F19.wireOp",EDGE,"E27.15.0.0")}),1.0]])]});
            var Q16;
            Q16=makeQuery(id+"F19.imprint","IMPRINT",FACE,{"disambiguationData":[TD([[makeQuery(id+"F19.imprint","IMPRINT",EDGE,{"derivedFrom":sQuery(id+"F19.wireOp",EDGE,"E27.16.0.0")}),1.0]])]});
            var Q17;
            Q17=makeQuery(id+"F19.imprint","IMPRINT",FACE,{"disambiguationData":[TD([[makeQuery(id+"F19.imprint","IMPRINT",EDGE,{"derivedFrom":sQuery(id+"F19.wireOp",EDGE,"E27.17.0.0")}),1.0]])]});
            var Q18;
            Q18=makeQuery(id+"F19.imprint","IMPRINT",FACE,{"disambiguationData":[TD([[makeQuery(id+"F19.imprint","IMPRINT",EDGE,{"derivedFrom":sQuery(id+"F19.wireOp",EDGE,"E27.18.0.0")}),1.0]])]});
            var Q19;
            Q19=makeQuery(id+"F19.imprint","IMPRINT",FACE,{"disambiguationData":[TD([[makeQuery(id+"F19.imprint","IMPRINT",EDGE,{"derivedFrom":sQuery(id+"F19.wireOp",EDGE,"E27.19.0.0")}),1.0]])]});
            var Q20;
            Q20=makeQuery(id+"F19.imprint","IMPRINT",FACE,{"disambiguationData":[TD([[makeQuery(id+"F19.imprint","IMPRINT",EDGE,{"derivedFrom":sQuery(id+"F19.wireOp",EDGE,"E27.20.0.0")}),1.0]])]});
            var Q21;
            Q21=makeQuery(id+"F19.imprint","IMPRINT",FACE,{"disambiguationData":[TD([[makeQuery(id+"F19.imprint","IMPRINT",EDGE,{"derivedFrom":sQuery(id+"F19.wireOp",EDGE,"E27.21.0.0")}),1.0]])]});
            var Q22;
            Q22=makeQuery(id+"F19.imprint","IMPRINT",FACE,{"disambiguationData":[TD([[makeQuery(id+"F19.imprint","IMPRINT",EDGE,{"derivedFrom":sQuery(id+"F19.wireOp",EDGE,"E27.22.0.0")}),1.0]])]});
            var Q23;
            Q23=makeQuery(id+"F19.imprint","IMPRINT",FACE,{"disambiguationData":[TD([[makeQuery(id+"F19.imprint","IMPRINT",EDGE,{"derivedFrom":sQuery(id+"F19.wireOp",EDGE,"E27.23.0.0")}),1.0]])]});
            var Q24;
            Q24=makeQuery(id+"F19.imprint","IMPRINT",FACE,{"disambiguationData":[TD([[makeQuery(id+"F19.imprint","IMPRINT",EDGE,{"derivedFrom":sQuery(id+"F19.wireOp",EDGE,"E27.24.0.0")}),1.0]])]});
            var Q25;
            Q25=makeQuery(id+"F19.imprint","IMPRINT",FACE,{"disambiguationData":[TD([[makeQuery(id+"F19.imprint","IMPRINT",EDGE,{"derivedFrom":sQuery(id+"F19.wireOp",EDGE,"E27.25.0.0")}),1.0]])]});
            var Q26;
            Q26=makeQuery(id+"F19.imprint","IMPRINT",FACE,{"disambiguationData":[TD([[makeQuery(id+"F19.imprint","IMPRINT",EDGE,{"derivedFrom":sQuery(id+"F19.wireOp",EDGE,"E27.26.0.0")}),1.0]])]});
            var Q27;
            Q27=makeQuery(id+"F19.imprint","IMPRINT",FACE,{"disambiguationData":[TD([[makeQuery(id+"F19.imprint","IMPRINT",EDGE,{"derivedFrom":sQuery(id+"F19.wireOp",EDGE,"E27.27.0.0")}),1.0]])]});
            var Q28;
            Q28=makeQuery(id+"F19.imprint","IMPRINT",FACE,{"disambiguationData":[TD([[makeQuery(id+"F19.imprint","IMPRINT",EDGE,{"derivedFrom":sQuery(id+"F19.wireOp",EDGE,"E27.28.0.0")}),1.0]])]});
            var Q29;
            Q29=makeQuery(id+"F19.imprint","IMPRINT",FACE,{"disambiguationData":[TD([[makeQuery(id+"F19.imprint","IMPRINT",EDGE,{"derivedFrom":sQuery(id+"F19.wireOp",EDGE,"E27.29.0.0")}),1.0]])]});
            var Q30;
            Q30=makeQuery(id+"F19.imprint","IMPRINT",FACE,{"disambiguationData":[TD([[makeQuery(id+"F19.imprint","IMPRINT",EDGE,{"derivedFrom":sQuery(id+"F19.wireOp",EDGE,"E27.30.0.0")}),1.0]])]});
            var Q31;
            Q31=makeQuery(id+"F19.imprint","IMPRINT",FACE,{"disambiguationData":[TD([[makeQuery(id+"F19.imprint","IMPRINT",EDGE,{"derivedFrom":sQuery(id+"F19.wireOp",EDGE,"E27.31.0.0")}),1.0]])]});
            var Q32;
            Q32=makeQuery(id+"F19.imprint","IMPRINT",FACE,{"disambiguationData":[TD([[makeQuery(id+"F19.imprint","IMPRINT",EDGE,{"derivedFrom":sQuery(id+"F19.wireOp",EDGE,"E27.34.0.0")}),1.0]])]});
            var Q33;
            Q33=makeQuery(id+"F19.imprint","IMPRINT",FACE,{"disambiguationData":[TD([[makeQuery(id+"F19.imprint","IMPRINT",EDGE,{"derivedFrom":sQuery(id+"F19.wireOp",EDGE,"E27.33.0.0")}),1.0]])]});
            var Q34;
            Q34=makeQuery(id+"F19.imprint","IMPRINT",FACE,{"disambiguationData":[TD([[makeQuery(id+"F19.imprint","IMPRINT",EDGE,{"derivedFrom":sQuery(id+"F19.wireOp",EDGE,"E27.32.0.0")}),1.0]])]});
            extrude(context, id + "F20", {"entities" : qUnion([Q0, Q1, Q2, Q3, Q4, Q5, Q6, Q7, Q8, Q9, Q10, Q11, Q12, Q13, Q14, Q15, Q16, Q17, Q18, Q19, Q20, Q21, Q22, Q23, Q24, Q25, Q26, Q27, Q28, Q29, Q30, Q31, Q32, Q33, Q34]), "operationType" : NewBodyOperationType.REMOVE, "oppositeDirection" : true, "depth" : 1.27 * mm, "offsetDistance" : 25.4 * mm});
        }
        {
            var Q0;
            Q0=makeQuery(id+"F8.imprint","IMPRINT",FACE,{"disambiguationData":[TD([[makeQuery(id+"F8.imprint","IMPRINT",EDGE,{"derivedFrom":sQuery(id+"F8.wireOp",EDGE,"E13")}),-1.0]])]});
            extrude(context, id + "F21", {"entities" : qUnion([Q0]), "operationType" : NewBodyOperationType.REMOVE, "oppositeDirection" : true, "depth" : 0.76 * mm, "offsetDistance" : 25.4 * mm});
        }
        {
            var Q0;
            Q0=makeQuery(id+"F21.boolean.opBoolean","COPY",FACE,{"derivedFrom":makeQuery(id+"F21.opExtrude","CAP_FACE",FACE,{"disambiguationData":[OSD([sQuery(id+"F8.wireOp",EDGE,"E13"),sQuery(id+"F8.wireOp",EDGE,"E14"),sQuery(id+"F8.wireOp",EDGE,"E15"),sQuery(id+"F8.wireOp",EDGE,"E16")])],"isStart":false})});
            extrude(context, id + "F22", {"entities" : qUnion([Q0]), "depth" : 0.25 * mm, "offsetDistance" : 25.4 * mm});
        }
        {
            var Q0;
            Q0=makeQuery(id+"F22.opExtrude","CAP_FACE",FACE,{"disambiguationData":[OSD([sQuery(id+"F8.wireOp",EDGE,"E13"),sQuery(id+"F8.wireOp",EDGE,"E14"),sQuery(id+"F8.wireOp",EDGE,"E15"),sQuery(id+"F8.wireOp",EDGE,"E16")])],"isStart":false});
            var sketch = newSketch(context, id + "F23", { "sketchPlane" : qUnion([Q0])});
            skLineSegment(sketch, "E28", {"start": v(30.18, 42.74) * mm, "end": v(30.18, -9.46) * mm, "construction": true});
            skCircle(sketch, "E29", {"center": v(30.18, 33.88) * mm, "radius": 5.72 * mm});
            skCircle(sketch, "E30", {"center": v(30.18, 18.97) * mm, "radius": 5.72 * mm});
            skCircle(sketch, "E31", {"center": v(30.18, 33.88) * mm, "radius": 4.45 * mm});
            skCircle(sketch, "E32", {"center": v(30.18, 18.97) * mm, "radius": 4.45 * mm});
            skSolve(sketch);
        }
        {
            var Q0;
            Q0=makeQuery(id+"F23.imprint","IMPRINT",FACE,{"disambiguationData":[TD([[makeQuery(id+"F23.imprint","IMPRINT",EDGE,{"derivedFrom":sQuery(id+"F23.wireOp",EDGE,"E30")}),1.0]])]});
            var Q1;
            Q1=makeQuery(id+"F23.imprint","IMPRINT",FACE,{"disambiguationData":[TD([[makeQuery(id+"F23.imprint","IMPRINT",EDGE,{"derivedFrom":sQuery(id+"F23.wireOp",EDGE,"E29")}),1.0]])]});
            var Q2;
            Q2=makeQuery(id+"F23.imprint","IMPRINT",FACE,{"disambiguationData":[TD([[makeQuery(id+"F23.imprint","IMPRINT",EDGE,{"derivedFrom":sQuery(id+"F23.wireOp",EDGE,"E31")}),1.0]])]});
            var Q3;
            Q3=makeQuery(id+"F23.imprint","IMPRINT",FACE,{"disambiguationData":[TD([[makeQuery(id+"F23.imprint","IMPRINT",EDGE,{"derivedFrom":sQuery(id+"F23.wireOp",EDGE,"E32")}),1.0]])]});
            extrude(context, id + "F24", {"entities" : qUnion([Q0, Q1, Q2, Q3]), "depth" : 1.27 * mm, "offsetDistance" : 25.4 * mm});
        }
        {
            var Q0;
            Q0=makeQuery(id+"F24.opExtrude","CAP_FACE",FACE,{"disambiguationData":[OSD([sQuery(id+"F23.wireOp",EDGE,"E29")])],"isStart":false});
            var sketch = newSketch(context, id + "F25", { "sketchPlane" : qUnion([Q0])});
            skCircle(sketch, "E33", {"center": v(30.18, 33.88) * mm, "radius": 4.45 * mm});
            skSolve(sketch);
        }
        {
            var Q0;
            Q0=makeQuery(id+"F24.opExtrude","CAP_FACE",FACE,{"disambiguationData":[OSD([sQuery(id+"F23.wireOp",EDGE,"E30")])],"isStart":false});
            var sketch = newSketch(context, id + "F26", { "sketchPlane" : qUnion([Q0])});
            skCircle(sketch, "E34", {"center": v(30.18, 18.97) * mm, "radius": 4.45 * mm});
            skSolve(sketch);
        }
        {
            var Q0;
            Q0=makeQuery(id+"F25.imprint","IMPRINT",FACE,{"disambiguationData":[TD([[makeQuery(id+"F25.imprint","IMPRINT",EDGE,{"derivedFrom":sQuery(id+"F25.wireOp",EDGE,"E33")}),1.0]])]});
            extrude(context, id + "F27", {"entities" : qUnion([Q0]), "operationType" : NewBodyOperationType.ADD, "depth" : 1.27 * mm, "offsetDistance" : 25.4 * mm});
        }
        {
            var Q0;
            Q0=makeQuery(id+"F26.imprint","IMPRINT",FACE,{"disambiguationData":[TD([[makeQuery(id+"F26.imprint","IMPRINT",EDGE,{"derivedFrom":sQuery(id+"F26.wireOp",EDGE,"E34")}),1.0]])]});
            extrude(context, id + "F28", {"entities" : qUnion([Q0]), "operationType" : NewBodyOperationType.ADD, "depth" : 1.27 * mm, "offsetDistance" : 25.4 * mm});
        }
        {
            var Q0;
            Q0=makeQuery(id+"F28.opExtrude","CAP_FACE",FACE,{"disambiguationData":[OSD([sQuery(id+"F26.wireOp",EDGE,"E34")])],"isStart":false});
            var sketch = newSketch(context, id + "F29", { "sketchPlane" : qUnion([Q0])});
            skLineSegment(sketch, "E35", {"start": v(26.57, 21.56) * mm, "end": v(32.8, 15.38) * mm});
            skLineSegment(sketch, "E36", {"start": v(27.6, 22.59) * mm, "end": v(33.94, 16.6) * mm});
            skSolve(sketch);
        }
        {
            var Q0;
            {var subQ0=sQuery(id+"F29.wireOp",EDGE,"E35");Q0=makeQuery(id+"F29.imprint","IMPRINT",FACE,{"disambiguationData":[TD([[makeQuery(id+"F29.imprint","IMPRINT",EDGE,{"derivedFrom":subQ0}),1.0]])]});}
            extrude(context, id + "F30", {"entities" : qUnion([Q0]), "operationType" : NewBodyOperationType.ADD, "depth" : 1.52 * mm, "offsetDistance" : 25.4 * mm});
        }
        {
            var Q0;
            Q0=makeQuery(id+"F27.opExtrude","CAP_FACE",FACE,{"disambiguationData":[OSD([sQuery(id+"F25.wireOp",EDGE,"E33")])],"isStart":false});
            var sketch = newSketch(context, id + "F31", { "sketchPlane" : qUnion([Q0])});
            skLineSegment(sketch, "E37", {"start": v(30.76, 38.3) * mm, "end": v(28.14, 29.94) * mm});
            skLineSegment(sketch, "E38", {"start": v(32.05, 37.92) * mm, "end": v(29.35, 29.52) * mm});
            skSolve(sketch);
        }
        {
            var Q0;
            {var subQ0=sQuery(id+"F31.wireOp",EDGE,"E37");Q0=makeQuery(id+"F31.imprint","IMPRINT",FACE,{"disambiguationData":[TD([[makeQuery(id+"F31.imprint","IMPRINT",EDGE,{"derivedFrom":subQ0}),1.0]])]});}
            extrude(context, id + "F32", {"entities" : qUnion([Q0]), "operationType" : NewBodyOperationType.ADD, "depth" : 1.52 * mm, "offsetDistance" : 25.4 * mm});
        }
        {
            var Q0;
            Q0=makeQuery(id+"F22.opExtrude","CAP_FACE",FACE,{"disambiguationData":[OSD([sQuery(id+"F8.wireOp",EDGE,"E13"),sQuery(id+"F8.wireOp",EDGE,"E14"),sQuery(id+"F8.wireOp",EDGE,"E15"),sQuery(id+"F8.wireOp",EDGE,"E16")])],"isStart":false});
            var sketch = newSketch(context, id + "F33", { "sketchPlane" : qUnion([Q0])});
            skLineSegment(sketch, "E39", {"start": v(22.63, 11.16) * mm, "end": v(37.68, 11.16) * mm});
            skLineSegment(sketch, "E40", {"start": v(37.68, 11.16) * mm, "end": v(37.68, 11.05) * mm});
            skLineSegment(sketch, "E41", {"start": v(37.68, 11.05) * mm, "end": v(22.63, 11.05) * mm});
            skLineSegment(sketch, "E42", {"start": v(22.63, 11.05) * mm, "end": v(22.63, 11.16) * mm});
            skLineSegment(sketch, "E43.1.0.0", {"start": v(22.63, 10.57) * mm, "end": v(22.63, 10.68) * mm});
            skLineSegment(sketch, "E43.1.0.1", {"start": v(37.68, 10.57) * mm, "end": v(22.63, 10.57) * mm});
            skLineSegment(sketch, "E43.1.0.2", {"start": v(22.63, 10.68) * mm, "end": v(37.68, 10.68) * mm});
            skLineSegment(sketch, "E43.1.0.3", {"start": v(37.68, 10.68) * mm, "end": v(37.68, 10.57) * mm});
            skLineSegment(sketch, "E43.2.0.0", {"start": v(22.63, 10.09) * mm, "end": v(22.63, 10.2) * mm});
            skLineSegment(sketch, "E43.2.0.1", {"start": v(37.68, 10.09) * mm, "end": v(22.63, 10.09) * mm});
            skLineSegment(sketch, "E43.2.0.2", {"start": v(22.63, 10.2) * mm, "end": v(37.68, 10.2) * mm});
            skLineSegment(sketch, "E43.2.0.3", {"start": v(37.68, 10.2) * mm, "end": v(37.68, 10.09) * mm});
            skLineSegment(sketch, "E43.3.0.0", {"start": v(22.63, 9.6) * mm, "end": v(22.63, 9.72) * mm});
            skLineSegment(sketch, "E43.3.0.1", {"start": v(37.68, 9.6) * mm, "end": v(22.63, 9.6) * mm});
            skLineSegment(sketch, "E43.3.0.2", {"start": v(22.63, 9.72) * mm, "end": v(37.68, 9.72) * mm});
            skLineSegment(sketch, "E43.3.0.3", {"start": v(37.68, 9.72) * mm, "end": v(37.68, 9.6) * mm});
            skLineSegment(sketch, "E43.4.0.0", {"start": v(22.63, 9.12) * mm, "end": v(22.63, 9.23) * mm});
            skLineSegment(sketch, "E43.4.0.1", {"start": v(37.68, 9.12) * mm, "end": v(22.63, 9.12) * mm});
            skLineSegment(sketch, "E43.4.0.2", {"start": v(22.63, 9.23) * mm, "end": v(37.68, 9.23) * mm});
            skLineSegment(sketch, "E43.4.0.3", {"start": v(37.68, 9.23) * mm, "end": v(37.68, 9.12) * mm});
            skLineSegment(sketch, "E43.5.0.0", {"start": v(22.63, 8.64) * mm, "end": v(22.63, 8.75) * mm});
            skLineSegment(sketch, "E43.5.0.1", {"start": v(37.68, 8.64) * mm, "end": v(22.63, 8.64) * mm});
            skLineSegment(sketch, "E43.5.0.2", {"start": v(22.63, 8.75) * mm, "end": v(37.68, 8.75) * mm});
            skLineSegment(sketch, "E43.5.0.3", {"start": v(37.68, 8.75) * mm, "end": v(37.68, 8.64) * mm});
            skLineSegment(sketch, "E43.6.0.0", {"start": v(22.63, 8.16) * mm, "end": v(22.63, 8.27) * mm});
            skLineSegment(sketch, "E43.6.0.1", {"start": v(37.68, 8.16) * mm, "end": v(22.63, 8.16) * mm});
            skLineSegment(sketch, "E43.6.0.2", {"start": v(22.63, 8.27) * mm, "end": v(37.68, 8.27) * mm});
            skLineSegment(sketch, "E43.6.0.3", {"start": v(37.68, 8.27) * mm, "end": v(37.68, 8.16) * mm});
            skLineSegment(sketch, "E43.7.0.0", {"start": v(22.63, 7.68) * mm, "end": v(22.63, 7.79) * mm});
            skLineSegment(sketch, "E43.7.0.1", {"start": v(37.68, 7.68) * mm, "end": v(22.63, 7.68) * mm});
            skLineSegment(sketch, "E43.7.0.2", {"start": v(22.63, 7.79) * mm, "end": v(37.68, 7.79) * mm});
            skLineSegment(sketch, "E43.7.0.3", {"start": v(37.68, 7.79) * mm, "end": v(37.68, 7.68) * mm});
            skLineSegment(sketch, "E43.8.0.0", {"start": v(22.63, 7.2) * mm, "end": v(22.63, 7.3) * mm});
            skLineSegment(sketch, "E43.8.0.1", {"start": v(37.68, 7.2) * mm, "end": v(22.63, 7.2) * mm});
            skLineSegment(sketch, "E43.8.0.2", {"start": v(22.63, 7.3) * mm, "end": v(37.68, 7.3) * mm});
            skLineSegment(sketch, "E43.8.0.3", {"start": v(37.68, 7.3) * mm, "end": v(37.68, 7.2) * mm});
            skLineSegment(sketch, "E43.9.0.0", {"start": v(22.63, 6.71) * mm, "end": v(22.63, 6.82) * mm});
            skLineSegment(sketch, "E43.9.0.1", {"start": v(37.68, 6.71) * mm, "end": v(22.63, 6.71) * mm});
            skLineSegment(sketch, "E43.9.0.2", {"start": v(22.63, 6.82) * mm, "end": v(37.68, 6.82) * mm});
            skLineSegment(sketch, "E43.9.0.3", {"start": v(37.68, 6.82) * mm, "end": v(37.68, 6.71) * mm});
            skLineSegment(sketch, "E43.10.0.0", {"start": v(22.63, 6.23) * mm, "end": v(22.63, 6.34) * mm});
            skLineSegment(sketch, "E43.10.0.1", {"start": v(37.68, 6.23) * mm, "end": v(22.63, 6.23) * mm});
            skLineSegment(sketch, "E43.10.0.2", {"start": v(22.63, 6.34) * mm, "end": v(37.68, 6.34) * mm});
            skLineSegment(sketch, "E43.10.0.3", {"start": v(37.68, 6.34) * mm, "end": v(37.68, 6.23) * mm});
            skLineSegment(sketch, "E43.11.0.0", {"start": v(22.63, 5.75) * mm, "end": v(22.63, 5.86) * mm});
            skLineSegment(sketch, "E43.11.0.1", {"start": v(37.68, 5.75) * mm, "end": v(22.63, 5.75) * mm});
            skLineSegment(sketch, "E43.11.0.2", {"start": v(22.63, 5.86) * mm, "end": v(37.68, 5.86) * mm});
            skLineSegment(sketch, "E43.11.0.3", {"start": v(37.68, 5.86) * mm, "end": v(37.68, 5.75) * mm});
            skLineSegment(sketch, "E43.12.0.0", {"start": v(22.63, 5.26) * mm, "end": v(22.63, 5.37) * mm});
            skLineSegment(sketch, "E43.12.0.1", {"start": v(37.68, 5.26) * mm, "end": v(22.63, 5.26) * mm});
            skLineSegment(sketch, "E43.12.0.2", {"start": v(22.63, 5.37) * mm, "end": v(37.68, 5.37) * mm});
            skLineSegment(sketch, "E43.12.0.3", {"start": v(37.68, 5.37) * mm, "end": v(37.68, 5.26) * mm});
            skLineSegment(sketch, "E43.13.0.0", {"start": v(22.63, 4.78) * mm, "end": v(22.63, 4.9) * mm});
            skLineSegment(sketch, "E43.13.0.1", {"start": v(37.68, 4.78) * mm, "end": v(22.63, 4.78) * mm});
            skLineSegment(sketch, "E43.13.0.2", {"start": v(22.63, 4.9) * mm, "end": v(37.68, 4.9) * mm});
            skLineSegment(sketch, "E43.13.0.3", {"start": v(37.68, 4.9) * mm, "end": v(37.68, 4.78) * mm});
            skLineSegment(sketch, "E43.14.0.0", {"start": v(22.63, 4.3) * mm, "end": v(22.63, 4.4) * mm});
            skLineSegment(sketch, "E43.14.0.1", {"start": v(37.68, 4.3) * mm, "end": v(22.63, 4.3) * mm});
            skLineSegment(sketch, "E43.14.0.2", {"start": v(22.63, 4.4) * mm, "end": v(37.68, 4.4) * mm});
            skLineSegment(sketch, "E43.14.0.3", {"start": v(37.68, 4.4) * mm, "end": v(37.68, 4.3) * mm});
            skLineSegment(sketch, "E43.15.0.0", {"start": v(22.63, 3.82) * mm, "end": v(22.63, 3.93) * mm});
            skLineSegment(sketch, "E43.15.0.1", {"start": v(37.67, 3.82) * mm, "end": v(22.63, 3.82) * mm});
            skLineSegment(sketch, "E43.15.0.2", {"start": v(22.63, 3.93) * mm, "end": v(37.67, 3.93) * mm});
            skLineSegment(sketch, "E43.15.0.3", {"start": v(37.67, 3.93) * mm, "end": v(37.67, 3.82) * mm});
            skLineSegment(sketch, "E43.16.0.0", {"start": v(22.63, 3.33) * mm, "end": v(22.63, 3.44) * mm});
            skLineSegment(sketch, "E43.16.0.1", {"start": v(37.67, 3.33) * mm, "end": v(22.63, 3.33) * mm});
            skLineSegment(sketch, "E43.16.0.2", {"start": v(22.63, 3.44) * mm, "end": v(37.67, 3.44) * mm});
            skLineSegment(sketch, "E43.16.0.3", {"start": v(37.67, 3.44) * mm, "end": v(37.67, 3.33) * mm});
            skLineSegment(sketch, "E43.17.0.0", {"start": v(22.63, 2.85) * mm, "end": v(22.63, 2.96) * mm});
            skLineSegment(sketch, "E43.17.0.1", {"start": v(37.67, 2.85) * mm, "end": v(22.63, 2.85) * mm});
            skLineSegment(sketch, "E43.17.0.2", {"start": v(22.63, 2.96) * mm, "end": v(37.67, 2.96) * mm});
            skLineSegment(sketch, "E43.17.0.3", {"start": v(37.67, 2.96) * mm, "end": v(37.67, 2.85) * mm});
            skLineSegment(sketch, "E43.18.0.0", {"start": v(22.63, 2.37) * mm, "end": v(22.63, 2.48) * mm});
            skLineSegment(sketch, "E43.18.0.1", {"start": v(37.67, 2.37) * mm, "end": v(22.63, 2.37) * mm});
            skLineSegment(sketch, "E43.18.0.2", {"start": v(22.63, 2.48) * mm, "end": v(37.67, 2.48) * mm});
            skLineSegment(sketch, "E43.18.0.3", {"start": v(37.67, 2.48) * mm, "end": v(37.67, 2.37) * mm});
            skLineSegment(sketch, "E43.19.0.0", {"start": v(22.63, 1.88) * mm, "end": v(22.63, 2) * mm});
            skLineSegment(sketch, "E43.19.0.1", {"start": v(37.67, 1.88) * mm, "end": v(22.63, 1.88) * mm});
            skLineSegment(sketch, "E43.19.0.2", {"start": v(22.63, 2) * mm, "end": v(37.67, 2) * mm});
            skLineSegment(sketch, "E43.19.0.3", {"start": v(37.67, 2) * mm, "end": v(37.67, 1.88) * mm});
            skLineSegment(sketch, "E43.20.0.0", {"start": v(22.62, 1.4) * mm, "end": v(22.62, 1.51) * mm});
            skLineSegment(sketch, "E43.20.0.1", {"start": v(37.67, 1.4) * mm, "end": v(22.62, 1.4) * mm});
            skLineSegment(sketch, "E43.20.0.2", {"start": v(22.62, 1.51) * mm, "end": v(37.67, 1.51) * mm});
            skLineSegment(sketch, "E43.20.0.3", {"start": v(37.67, 1.51) * mm, "end": v(37.67, 1.4) * mm});
            skLineSegment(sketch, "E43.21.0.0", {"start": v(22.62, 0.92) * mm, "end": v(22.62, 1.03) * mm});
            skLineSegment(sketch, "E43.21.0.1", {"start": v(37.67, 0.92) * mm, "end": v(22.62, 0.92) * mm});
            skLineSegment(sketch, "E43.21.0.2", {"start": v(22.62, 1.03) * mm, "end": v(37.67, 1.03) * mm});
            skLineSegment(sketch, "E43.21.0.3", {"start": v(37.67, 1.03) * mm, "end": v(37.67, 0.92) * mm});
            skLineSegment(sketch, "E43.22.0.0", {"start": v(22.62, 0.44) * mm, "end": v(22.62, 0.55) * mm});
            skLineSegment(sketch, "E43.22.0.1", {"start": v(37.67, 0.44) * mm, "end": v(22.62, 0.44) * mm});
            skLineSegment(sketch, "E43.22.0.2", {"start": v(22.62, 0.55) * mm, "end": v(37.67, 0.55) * mm});
            skLineSegment(sketch, "E43.22.0.3", {"start": v(37.67, 0.55) * mm, "end": v(37.67, 0.44) * mm});
            skLineSegment(sketch, "E43.23.0.0", {"start": v(22.62, -0.05) * mm, "end": v(22.62, 0.07) * mm});
            skLineSegment(sketch, "E43.23.0.1", {"start": v(37.67, -0.05) * mm, "end": v(22.62, -0.05) * mm});
            skLineSegment(sketch, "E43.23.0.2", {"start": v(22.62, 0.07) * mm, "end": v(37.67, 0.07) * mm});
            skLineSegment(sketch, "E43.23.0.3", {"start": v(37.67, 0.07) * mm, "end": v(37.67, -0.05) * mm});
            skLineSegment(sketch, "E43.24.0.0", {"start": v(22.62, -0.53) * mm, "end": v(22.62, -0.42) * mm});
            skLineSegment(sketch, "E43.24.0.1", {"start": v(37.67, -0.53) * mm, "end": v(22.62, -0.53) * mm});
            skLineSegment(sketch, "E43.24.0.2", {"start": v(22.62, -0.42) * mm, "end": v(37.67, -0.42) * mm});
            skLineSegment(sketch, "E43.24.0.3", {"start": v(37.67, -0.42) * mm, "end": v(37.67, -0.53) * mm});
            skLineSegment(sketch, "E43.25.0.0", {"start": v(22.62, -1.01) * mm, "end": v(22.62, -0.9) * mm});
            skLineSegment(sketch, "E43.25.0.1", {"start": v(37.67, -1.01) * mm, "end": v(22.62, -1.01) * mm});
            skLineSegment(sketch, "E43.25.0.2", {"start": v(22.62, -0.9) * mm, "end": v(37.67, -0.9) * mm});
            skLineSegment(sketch, "E43.25.0.3", {"start": v(37.67, -0.9) * mm, "end": v(37.67, -1.01) * mm});
            skLineSegment(sketch, "E43.26.0.0", {"start": v(22.62, -1.5) * mm, "end": v(22.62, -1.38) * mm});
            skLineSegment(sketch, "E43.26.0.1", {"start": v(37.67, -1.5) * mm, "end": v(22.62, -1.5) * mm});
            skLineSegment(sketch, "E43.26.0.2", {"start": v(22.62, -1.38) * mm, "end": v(37.67, -1.38) * mm});
            skLineSegment(sketch, "E43.26.0.3", {"start": v(37.67, -1.38) * mm, "end": v(37.67, -1.5) * mm});
            skLineSegment(sketch, "E43.27.0.0", {"start": v(22.62, -1.98) * mm, "end": v(22.62, -1.87) * mm});
            skLineSegment(sketch, "E43.27.0.1", {"start": v(37.67, -1.98) * mm, "end": v(22.62, -1.98) * mm});
            skLineSegment(sketch, "E43.27.0.2", {"start": v(22.62, -1.87) * mm, "end": v(37.67, -1.87) * mm});
            skLineSegment(sketch, "E43.27.0.3", {"start": v(37.67, -1.87) * mm, "end": v(37.67, -1.98) * mm});
            skLineSegment(sketch, "E43.28.0.0", {"start": v(22.62, -2.46) * mm, "end": v(22.62, -2.35) * mm});
            skLineSegment(sketch, "E43.28.0.1", {"start": v(37.67, -2.46) * mm, "end": v(22.62, -2.46) * mm});
            skLineSegment(sketch, "E43.28.0.2", {"start": v(22.62, -2.35) * mm, "end": v(37.67, -2.35) * mm});
            skLineSegment(sketch, "E43.28.0.3", {"start": v(37.67, -2.35) * mm, "end": v(37.67, -2.46) * mm});
            skLineSegment(sketch, "E43.29.0.0", {"start": v(22.62, -2.94) * mm, "end": v(22.62, -2.83) * mm});
            skLineSegment(sketch, "E43.29.0.1", {"start": v(37.67, -2.94) * mm, "end": v(22.62, -2.94) * mm});
            skLineSegment(sketch, "E43.29.0.2", {"start": v(22.62, -2.83) * mm, "end": v(37.67, -2.83) * mm});
            skLineSegment(sketch, "E43.29.0.3", {"start": v(37.67, -2.83) * mm, "end": v(37.67, -2.94) * mm});
            skLineSegment(sketch, "E43.30.0.0", {"start": v(22.62, -3.42) * mm, "end": v(22.62, -3.31) * mm});
            skLineSegment(sketch, "E43.30.0.1", {"start": v(37.67, -3.42) * mm, "end": v(22.62, -3.42) * mm});
            skLineSegment(sketch, "E43.30.0.2", {"start": v(22.62, -3.31) * mm, "end": v(37.67, -3.31) * mm});
            skLineSegment(sketch, "E43.30.0.3", {"start": v(37.67, -3.31) * mm, "end": v(37.67, -3.42) * mm});
            skLineSegment(sketch, "E43.31.0.0", {"start": v(22.62, -3.9) * mm, "end": v(22.62, -3.8) * mm});
            skLineSegment(sketch, "E43.31.0.1", {"start": v(37.67, -3.9) * mm, "end": v(22.62, -3.9) * mm});
            skLineSegment(sketch, "E43.31.0.2", {"start": v(22.62, -3.8) * mm, "end": v(37.67, -3.8) * mm});
            skLineSegment(sketch, "E43.31.0.3", {"start": v(37.67, -3.8) * mm, "end": v(37.67, -3.9) * mm});
            skLineSegment(sketch, "E43.32.0.0", {"start": v(22.62, -4.39) * mm, "end": v(22.62, -4.28) * mm});
            skLineSegment(sketch, "E43.32.0.1", {"start": v(37.67, -4.39) * mm, "end": v(22.62, -4.39) * mm});
            skLineSegment(sketch, "E43.32.0.2", {"start": v(22.62, -4.28) * mm, "end": v(37.67, -4.28) * mm});
            skLineSegment(sketch, "E43.32.0.3", {"start": v(37.67, -4.28) * mm, "end": v(37.67, -4.39) * mm});
            skLineSegment(sketch, "E43.33.0.0", {"start": v(22.62, -4.87) * mm, "end": v(22.62, -4.76) * mm});
            skLineSegment(sketch, "E43.33.0.1", {"start": v(37.67, -4.87) * mm, "end": v(22.62, -4.87) * mm});
            skLineSegment(sketch, "E43.33.0.2", {"start": v(22.62, -4.76) * mm, "end": v(37.67, -4.76) * mm});
            skLineSegment(sketch, "E43.33.0.3", {"start": v(37.67, -4.76) * mm, "end": v(37.67, -4.87) * mm});
            skLineSegment(sketch, "E43.34.0.0", {"start": v(22.62, -5.35) * mm, "end": v(22.62, -5.24) * mm});
            skLineSegment(sketch, "E43.34.0.1", {"start": v(37.67, -5.35) * mm, "end": v(22.62, -5.35) * mm});
            skLineSegment(sketch, "E43.34.0.2", {"start": v(22.62, -5.24) * mm, "end": v(37.67, -5.24) * mm});
            skLineSegment(sketch, "E43.34.0.3", {"start": v(37.67, -5.24) * mm, "end": v(37.67, -5.35) * mm});
            skLineSegment(sketch, "E43.35.0.0", {"start": v(22.62, -5.84) * mm, "end": v(22.62, -5.73) * mm});
            skLineSegment(sketch, "E43.35.0.1", {"start": v(37.67, -5.84) * mm, "end": v(22.62, -5.84) * mm});
            skLineSegment(sketch, "E43.35.0.2", {"start": v(22.62, -5.73) * mm, "end": v(37.67, -5.73) * mm});
            skLineSegment(sketch, "E43.35.0.3", {"start": v(37.67, -5.73) * mm, "end": v(37.67, -5.84) * mm});
            skLineSegment(sketch, "E43.36.0.0", {"start": v(22.62, -6.32) * mm, "end": v(22.62, -6.2) * mm});
            skLineSegment(sketch, "E43.36.0.1", {"start": v(37.67, -6.32) * mm, "end": v(22.62, -6.32) * mm});
            skLineSegment(sketch, "E43.36.0.2", {"start": v(22.62, -6.2) * mm, "end": v(37.67, -6.2) * mm});
            skLineSegment(sketch, "E43.36.0.3", {"start": v(37.67, -6.2) * mm, "end": v(37.67, -6.32) * mm});
            skLineSegment(sketch, "E43.37.0.0", {"start": v(22.62, -6.8) * mm, "end": v(22.62, -6.7) * mm});
            skLineSegment(sketch, "E43.37.0.1", {"start": v(37.67, -6.8) * mm, "end": v(22.62, -6.8) * mm});
            skLineSegment(sketch, "E43.37.0.2", {"start": v(22.62, -6.7) * mm, "end": v(37.67, -6.7) * mm});
            skLineSegment(sketch, "E43.37.0.3", {"start": v(37.67, -6.7) * mm, "end": v(37.67, -6.8) * mm});
            skLineSegment(sketch, "E43.38.0.0", {"start": v(22.62, -7.28) * mm, "end": v(22.62, -7.17) * mm});
            skLineSegment(sketch, "E43.38.0.1", {"start": v(37.67, -7.28) * mm, "end": v(22.62, -7.28) * mm});
            skLineSegment(sketch, "E43.38.0.2", {"start": v(22.62, -7.17) * mm, "end": v(37.67, -7.17) * mm});
            skLineSegment(sketch, "E43.38.0.3", {"start": v(37.67, -7.17) * mm, "end": v(37.67, -7.28) * mm});
            skLineSegment(sketch, "E43.39.0.0", {"start": v(22.62, -7.77) * mm, "end": v(22.62, -7.66) * mm});
            skLineSegment(sketch, "E43.39.0.1", {"start": v(37.66, -7.77) * mm, "end": v(22.62, -7.77) * mm});
            skLineSegment(sketch, "E43.39.0.2", {"start": v(22.62, -7.66) * mm, "end": v(37.66, -7.66) * mm});
            skLineSegment(sketch, "E43.39.0.3", {"start": v(37.66, -7.66) * mm, "end": v(37.66, -7.77) * mm});
            skLineSegment(sketch, "E43.direction1", {"start": v(22.63, 11.05) * mm, "end": v(22.63, 10.57) * mm, "construction": true});
            skSolve(sketch);
        }
        {
            var Q0;
            Q0 = qSketchRegion(id + "F33", true);
            extrude(context, id + "F34", {"entities" : qUnion([Q0]), "operationType" : NewBodyOperationType.REMOVE, "oppositeDirection" : true, "depth" : 0.25 * mm, "offsetDistance" : 25.4 * mm});
        }
        {
            var Q0;
            Q0=makeQuery(id+"F5.boolean.opBoolean","COPY",FACE,{"derivedFrom":makeQuery(id+"F5.opExtrude","CAP_FACE",FACE,{"disambiguationData":[OSD([sQuery(id+"F3.wireOp",EDGE,"E9"),sQuery(id+"F3.wireOp",EDGE,"E10"),sQuery(id+"F3.wireOp",EDGE,"E11"),sQuery(id+"F3.wireOp",EDGE,"E12")])],"isStart":false})});
            extrude(context, id + "F35", {"entities" : qUnion([Q0]), "depth" : 0.03 * mm, "offsetDistance" : 25.4 * mm});
        }
        {
            var Q0;
            Q0=makeQuery(id+"F11.opChamfer","BLEND_FACE",FACE,{"disambiguationData":[OSD([sQuery(id+"F9.wireOp",EDGE,"E21.bottom")])]});
            var sketch = newSketch(context, id + "F36", { "sketchPlane" : qUnion([Q0])});
            skLineSegment(sketch, "E44", {"start": v(-6.1, 10.7) * mm, "end": v(-6.1, -3.17) * mm});
            skLineSegment(sketch, "E45", {"start": v(-6.44, -3.17) * mm, "end": v(-6.1, -3.17) * mm});
            skLineSegment(sketch, "E46", {"start": v(-6.44, -3.17) * mm, "end": v(-6.44, 10.7) * mm});
            skLineSegment(sketch, "E47", {"start": v(-6.1, 10.7) * mm, "end": v(-6.44, 10.7) * mm});
            skLineSegment(sketch, "E48.1.0.0", {"start": v(-5.42, -3.17) * mm, "end": v(-5.08, -3.17) * mm});
            skLineSegment(sketch, "E48.1.0.1", {"start": v(-5.08, 10.7) * mm, "end": v(-5.08, -3.17) * mm});
            skLineSegment(sketch, "E48.1.0.2", {"start": v(-5.42, -3.17) * mm, "end": v(-5.42, 10.7) * mm});
            skLineSegment(sketch, "E48.1.0.3", {"start": v(-5.08, 10.7) * mm, "end": v(-5.42, 10.7) * mm});
            skLineSegment(sketch, "E48.2.0.0", {"start": v(-4.4, -3.17) * mm, "end": v(-4.06, -3.17) * mm});
            skLineSegment(sketch, "E48.2.0.1", {"start": v(-4.06, 10.7) * mm, "end": v(-4.06, -3.17) * mm});
            skLineSegment(sketch, "E48.2.0.2", {"start": v(-4.4, -3.17) * mm, "end": v(-4.4, 10.7) * mm});
            skLineSegment(sketch, "E48.2.0.3", {"start": v(-4.06, 10.7) * mm, "end": v(-4.4, 10.7) * mm});
            skLineSegment(sketch, "E48.3.0.0", {"start": v(-3.4, -3.17) * mm, "end": v(-3.05, -3.17) * mm});
            skLineSegment(sketch, "E48.3.0.1", {"start": v(-3.05, 10.7) * mm, "end": v(-3.05, -3.17) * mm});
            skLineSegment(sketch, "E48.3.0.2", {"start": v(-3.4, -3.17) * mm, "end": v(-3.4, 10.7) * mm});
            skLineSegment(sketch, "E48.3.0.3", {"start": v(-3.05, 10.7) * mm, "end": v(-3.4, 10.7) * mm});
            skLineSegment(sketch, "E48.4.0.0", {"start": v(-2.38, -3.17) * mm, "end": v(-2.03, -3.17) * mm});
            skLineSegment(sketch, "E48.4.0.1", {"start": v(-2.03, 10.7) * mm, "end": v(-2.03, -3.17) * mm});
            skLineSegment(sketch, "E48.4.0.2", {"start": v(-2.38, -3.17) * mm, "end": v(-2.38, 10.7) * mm});
            skLineSegment(sketch, "E48.4.0.3", {"start": v(-2.03, 10.7) * mm, "end": v(-2.38, 10.7) * mm});
            skLineSegment(sketch, "E48.5.0.0", {"start": v(-1.36, -3.17) * mm, "end": v(-1.02, -3.17) * mm});
            skLineSegment(sketch, "E48.5.0.1", {"start": v(-1.02, 10.7) * mm, "end": v(-1.02, -3.17) * mm});
            skLineSegment(sketch, "E48.5.0.2", {"start": v(-1.36, -3.17) * mm, "end": v(-1.36, 10.7) * mm});
            skLineSegment(sketch, "E48.5.0.3", {"start": v(-1.02, 10.7) * mm, "end": v(-1.36, 10.7) * mm});
            skLineSegment(sketch, "E48.6.0.0", {"start": v(-0.34, -3.17) * mm, "end": v(0, -3.17) * mm});
            skLineSegment(sketch, "E48.6.0.1", {"start": v(0, 10.7) * mm, "end": v(0, -3.17) * mm});
            skLineSegment(sketch, "E48.6.0.2", {"start": v(-0.34, -3.17) * mm, "end": v(-0.34, 10.7) * mm});
            skLineSegment(sketch, "E48.6.0.3", {"start": v(0, 10.7) * mm, "end": v(-0.34, 10.7) * mm});
            skLineSegment(sketch, "E48.7.0.0", {"start": v(0.67, -3.17) * mm, "end": v(1.02, -3.17) * mm});
            skLineSegment(sketch, "E48.7.0.1", {"start": v(1.02, 10.7) * mm, "end": v(1.02, -3.17) * mm});
            skLineSegment(sketch, "E48.7.0.2", {"start": v(0.67, -3.17) * mm, "end": v(0.67, 10.7) * mm});
            skLineSegment(sketch, "E48.7.0.3", {"start": v(1.02, 10.7) * mm, "end": v(0.67, 10.7) * mm});
            skLineSegment(sketch, "E48.8.0.0", {"start": v(1.69, -3.17) * mm, "end": v(2.03, -3.17) * mm});
            skLineSegment(sketch, "E48.8.0.1", {"start": v(2.03, 10.7) * mm, "end": v(2.03, -3.17) * mm});
            skLineSegment(sketch, "E48.8.0.2", {"start": v(1.69, -3.17) * mm, "end": v(1.69, 10.7) * mm});
            skLineSegment(sketch, "E48.8.0.3", {"start": v(2.03, 10.7) * mm, "end": v(1.69, 10.7) * mm});
            skLineSegment(sketch, "E48.9.0.0", {"start": v(2.7, -3.17) * mm, "end": v(3.05, -3.17) * mm});
            skLineSegment(sketch, "E48.9.0.1", {"start": v(3.05, 10.7) * mm, "end": v(3.05, -3.17) * mm});
            skLineSegment(sketch, "E48.9.0.2", {"start": v(2.7, -3.17) * mm, "end": v(2.7, 10.7) * mm});
            skLineSegment(sketch, "E48.9.0.3", {"start": v(3.05, 10.7) * mm, "end": v(2.7, 10.7) * mm});
            skLineSegment(sketch, "E48.10.0.0", {"start": v(3.72, -3.17) * mm, "end": v(4.06, -3.17) * mm});
            skLineSegment(sketch, "E48.10.0.1", {"start": v(4.06, 10.7) * mm, "end": v(4.06, -3.17) * mm});
            skLineSegment(sketch, "E48.10.0.2", {"start": v(3.72, -3.17) * mm, "end": v(3.72, 10.7) * mm});
            skLineSegment(sketch, "E48.10.0.3", {"start": v(4.06, 10.7) * mm, "end": v(3.72, 10.7) * mm});
            skLineSegment(sketch, "E48.11.0.0", {"start": v(4.74, -3.17) * mm, "end": v(5.08, -3.17) * mm});
            skLineSegment(sketch, "E48.11.0.1", {"start": v(5.08, 10.7) * mm, "end": v(5.08, -3.17) * mm});
            skLineSegment(sketch, "E48.11.0.2", {"start": v(4.74, -3.17) * mm, "end": v(4.74, 10.7) * mm});
            skLineSegment(sketch, "E48.11.0.3", {"start": v(5.08, 10.7) * mm, "end": v(4.74, 10.7) * mm});
            skLineSegment(sketch, "E48.12.0.0", {"start": v(5.75, -3.17) * mm, "end": v(6.1, -3.17) * mm});
            skLineSegment(sketch, "E48.12.0.1", {"start": v(6.1, 10.7) * mm, "end": v(6.1, -3.17) * mm});
            skLineSegment(sketch, "E48.12.0.2", {"start": v(5.75, -3.17) * mm, "end": v(5.75, 10.7) * mm});
            skLineSegment(sketch, "E48.12.0.3", {"start": v(6.1, 10.7) * mm, "end": v(5.75, 10.7) * mm});
            skLineSegment(sketch, "E48.13.0.0", {"start": v(6.77, -3.17) * mm, "end": v(7.11, -3.17) * mm});
            skLineSegment(sketch, "E48.13.0.1", {"start": v(7.11, 10.7) * mm, "end": v(7.11, -3.17) * mm});
            skLineSegment(sketch, "E48.13.0.2", {"start": v(6.77, -3.17) * mm, "end": v(6.77, 10.7) * mm});
            skLineSegment(sketch, "E48.13.0.3", {"start": v(7.11, 10.7) * mm, "end": v(6.77, 10.7) * mm});
            skLineSegment(sketch, "E48.14.0.0", {"start": v(7.78, -3.17) * mm, "end": v(8.13, -3.17) * mm});
            skLineSegment(sketch, "E48.14.0.1", {"start": v(8.13, 10.7) * mm, "end": v(8.13, -3.17) * mm});
            skLineSegment(sketch, "E48.14.0.2", {"start": v(7.78, -3.17) * mm, "end": v(7.78, 10.7) * mm});
            skLineSegment(sketch, "E48.14.0.3", {"start": v(8.13, 10.7) * mm, "end": v(7.78, 10.7) * mm});
            skLineSegment(sketch, "E48.15.0.0", {"start": v(8.8, -3.17) * mm, "end": v(9.14, -3.17) * mm});
            skLineSegment(sketch, "E48.15.0.1", {"start": v(9.14, 10.7) * mm, "end": v(9.14, -3.17) * mm});
            skLineSegment(sketch, "E48.15.0.2", {"start": v(8.8, -3.17) * mm, "end": v(8.8, 10.7) * mm});
            skLineSegment(sketch, "E48.15.0.3", {"start": v(9.14, 10.7) * mm, "end": v(8.8, 10.7) * mm});
            skLineSegment(sketch, "E48.16.0.0", {"start": v(9.82, -3.17) * mm, "end": v(10.16, -3.17) * mm});
            skLineSegment(sketch, "E48.16.0.1", {"start": v(10.16, 10.7) * mm, "end": v(10.16, -3.17) * mm});
            skLineSegment(sketch, "E48.16.0.2", {"start": v(9.82, -3.17) * mm, "end": v(9.82, 10.7) * mm});
            skLineSegment(sketch, "E48.16.0.3", {"start": v(10.16, 10.7) * mm, "end": v(9.82, 10.7) * mm});
            skLineSegment(sketch, "E48.17.0.0", {"start": v(10.83, -3.17) * mm, "end": v(11.18, -3.17) * mm});
            skLineSegment(sketch, "E48.17.0.1", {"start": v(11.18, 10.7) * mm, "end": v(11.18, -3.17) * mm});
            skLineSegment(sketch, "E48.17.0.2", {"start": v(10.83, -3.17) * mm, "end": v(10.83, 10.7) * mm});
            skLineSegment(sketch, "E48.17.0.3", {"start": v(11.18, 10.7) * mm, "end": v(10.83, 10.7) * mm});
            skLineSegment(sketch, "E48.18.0.0", {"start": v(11.85, -3.17) * mm, "end": v(12.2, -3.17) * mm});
            skLineSegment(sketch, "E48.18.0.1", {"start": v(12.2, 10.7) * mm, "end": v(12.2, -3.17) * mm});
            skLineSegment(sketch, "E48.18.0.2", {"start": v(11.85, -3.17) * mm, "end": v(11.85, 10.7) * mm});
            skLineSegment(sketch, "E48.18.0.3", {"start": v(12.2, 10.7) * mm, "end": v(11.85, 10.7) * mm});
            skLineSegment(sketch, "E48.19.0.0", {"start": v(12.86, -3.17) * mm, "end": v(13.2, -3.17) * mm});
            skLineSegment(sketch, "E48.19.0.1", {"start": v(13.2, 10.7) * mm, "end": v(13.2, -3.17) * mm});
            skLineSegment(sketch, "E48.19.0.2", {"start": v(12.86, -3.17) * mm, "end": v(12.86, 10.7) * mm});
            skLineSegment(sketch, "E48.19.0.3", {"start": v(13.2, 10.7) * mm, "end": v(12.86, 10.7) * mm});
            skLineSegment(sketch, "E48.20.0.0", {"start": v(13.88, -3.17) * mm, "end": v(14.22, -3.17) * mm});
            skLineSegment(sketch, "E48.20.0.1", {"start": v(14.22, 10.7) * mm, "end": v(14.22, -3.17) * mm});
            skLineSegment(sketch, "E48.20.0.2", {"start": v(13.88, -3.17) * mm, "end": v(13.88, 10.7) * mm});
            skLineSegment(sketch, "E48.20.0.3", {"start": v(14.22, 10.7) * mm, "end": v(13.88, 10.7) * mm});
            skLineSegment(sketch, "E48.21.0.0", {"start": v(14.9, -3.17) * mm, "end": v(15.24, -3.17) * mm});
            skLineSegment(sketch, "E48.21.0.1", {"start": v(15.24, 10.7) * mm, "end": v(15.24, -3.17) * mm});
            skLineSegment(sketch, "E48.21.0.2", {"start": v(14.9, -3.17) * mm, "end": v(14.9, 10.7) * mm});
            skLineSegment(sketch, "E48.21.0.3", {"start": v(15.24, 10.7) * mm, "end": v(14.9, 10.7) * mm});
            skLineSegment(sketch, "E48.22.0.0", {"start": v(15.91, -3.17) * mm, "end": v(16.26, -3.17) * mm});
            skLineSegment(sketch, "E48.22.0.1", {"start": v(16.26, 10.7) * mm, "end": v(16.26, -3.17) * mm});
            skLineSegment(sketch, "E48.22.0.2", {"start": v(15.91, -3.17) * mm, "end": v(15.91, 10.7) * mm});
            skLineSegment(sketch, "E48.22.0.3", {"start": v(16.26, 10.7) * mm, "end": v(15.91, 10.7) * mm});
            skLineSegment(sketch, "E48.23.0.0", {"start": v(16.93, -3.17) * mm, "end": v(17.27, -3.17) * mm});
            skLineSegment(sketch, "E48.23.0.1", {"start": v(17.27, 10.7) * mm, "end": v(17.27, -3.17) * mm});
            skLineSegment(sketch, "E48.23.0.2", {"start": v(16.93, -3.17) * mm, "end": v(16.93, 10.7) * mm});
            skLineSegment(sketch, "E48.23.0.3", {"start": v(17.27, 10.7) * mm, "end": v(16.93, 10.7) * mm});
            skLineSegment(sketch, "E48.24.0.0", {"start": v(17.94, -3.17) * mm, "end": v(18.29, -3.17) * mm});
            skLineSegment(sketch, "E48.24.0.1", {"start": v(18.29, 10.7) * mm, "end": v(18.29, -3.17) * mm});
            skLineSegment(sketch, "E48.24.0.2", {"start": v(17.94, -3.17) * mm, "end": v(17.94, 10.7) * mm});
            skLineSegment(sketch, "E48.24.0.3", {"start": v(18.29, 10.7) * mm, "end": v(17.94, 10.7) * mm});
            skLineSegment(sketch, "E48.25.0.0", {"start": v(18.96, -3.17) * mm, "end": v(19.3, -3.17) * mm});
            skLineSegment(sketch, "E48.25.0.1", {"start": v(19.3, 10.7) * mm, "end": v(19.3, -3.17) * mm});
            skLineSegment(sketch, "E48.25.0.2", {"start": v(18.96, -3.17) * mm, "end": v(18.96, 10.7) * mm});
            skLineSegment(sketch, "E48.25.0.3", {"start": v(19.3, 10.7) * mm, "end": v(18.96, 10.7) * mm});
            skLineSegment(sketch, "E48.26.0.0", {"start": v(19.98, -3.17) * mm, "end": v(20.32, -3.17) * mm});
            skLineSegment(sketch, "E48.26.0.1", {"start": v(20.32, 10.7) * mm, "end": v(20.32, -3.17) * mm});
            skLineSegment(sketch, "E48.26.0.2", {"start": v(19.98, -3.17) * mm, "end": v(19.98, 10.7) * mm});
            skLineSegment(sketch, "E48.26.0.3", {"start": v(20.32, 10.7) * mm, "end": v(19.98, 10.7) * mm});
            skLineSegment(sketch, "E48.27.0.0", {"start": v(21, -3.17) * mm, "end": v(21.34, -3.17) * mm});
            skLineSegment(sketch, "E48.27.0.1", {"start": v(21.34, 10.7) * mm, "end": v(21.34, -3.17) * mm});
            skLineSegment(sketch, "E48.27.0.2", {"start": v(21, -3.17) * mm, "end": v(21, 10.7) * mm});
            skLineSegment(sketch, "E48.27.0.3", {"start": v(21.34, 10.7) * mm, "end": v(21, 10.7) * mm});
            skLineSegment(sketch, "E48.28.0.0", {"start": v(22, -3.17) * mm, "end": v(22.35, -3.17) * mm});
            skLineSegment(sketch, "E48.28.0.1", {"start": v(22.35, 10.7) * mm, "end": v(22.35, -3.17) * mm});
            skLineSegment(sketch, "E48.28.0.2", {"start": v(22, -3.17) * mm, "end": v(22, 10.7) * mm});
            skLineSegment(sketch, "E48.28.0.3", {"start": v(22.35, 10.7) * mm, "end": v(22, 10.7) * mm});
            skLineSegment(sketch, "E48.29.0.0", {"start": v(23.02, -3.17) * mm, "end": v(23.37, -3.17) * mm});
            skLineSegment(sketch, "E48.29.0.1", {"start": v(23.37, 10.7) * mm, "end": v(23.37, -3.17) * mm});
            skLineSegment(sketch, "E48.29.0.2", {"start": v(23.02, -3.17) * mm, "end": v(23.02, 10.7) * mm});
            skLineSegment(sketch, "E48.29.0.3", {"start": v(23.37, 10.7) * mm, "end": v(23.02, 10.7) * mm});
            skLineSegment(sketch, "E48.30.0.0", {"start": v(24.04, -3.17) * mm, "end": v(24.38, -3.17) * mm});
            skLineSegment(sketch, "E48.30.0.1", {"start": v(24.38, 10.7) * mm, "end": v(24.38, -3.17) * mm});
            skLineSegment(sketch, "E48.30.0.2", {"start": v(24.04, -3.17) * mm, "end": v(24.04, 10.7) * mm});
            skLineSegment(sketch, "E48.30.0.3", {"start": v(24.38, 10.7) * mm, "end": v(24.04, 10.7) * mm});
            skLineSegment(sketch, "E48.31.0.0", {"start": v(25.06, -3.17) * mm, "end": v(25.4, -3.17) * mm});
            skLineSegment(sketch, "E48.31.0.1", {"start": v(25.4, 10.7) * mm, "end": v(25.4, -3.17) * mm});
            skLineSegment(sketch, "E48.31.0.2", {"start": v(25.06, -3.17) * mm, "end": v(25.06, 10.7) * mm});
            skLineSegment(sketch, "E48.31.0.3", {"start": v(25.4, 10.7) * mm, "end": v(25.06, 10.7) * mm});
            skLineSegment(sketch, "E48.32.0.0", {"start": v(26.07, -3.17) * mm, "end": v(26.42, -3.17) * mm});
            skLineSegment(sketch, "E48.32.0.1", {"start": v(26.42, 10.7) * mm, "end": v(26.42, -3.17) * mm});
            skLineSegment(sketch, "E48.32.0.2", {"start": v(26.07, -3.17) * mm, "end": v(26.07, 10.7) * mm});
            skLineSegment(sketch, "E48.32.0.3", {"start": v(26.42, 10.7) * mm, "end": v(26.07, 10.7) * mm});
            skLineSegment(sketch, "E48.33.0.0", {"start": v(27.09, -3.17) * mm, "end": v(27.43, -3.17) * mm});
            skLineSegment(sketch, "E48.33.0.1", {"start": v(27.43, 10.7) * mm, "end": v(27.43, -3.17) * mm});
            skLineSegment(sketch, "E48.33.0.2", {"start": v(27.09, -3.17) * mm, "end": v(27.09, 10.7) * mm});
            skLineSegment(sketch, "E48.33.0.3", {"start": v(27.43, 10.7) * mm, "end": v(27.09, 10.7) * mm});
            skLineSegment(sketch, "E48.34.0.0", {"start": v(28.1, -3.17) * mm, "end": v(28.45, -3.17) * mm});
            skLineSegment(sketch, "E48.34.0.1", {"start": v(28.45, 10.7) * mm, "end": v(28.45, -3.17) * mm});
            skLineSegment(sketch, "E48.34.0.2", {"start": v(28.1, -3.17) * mm, "end": v(28.1, 10.7) * mm});
            skLineSegment(sketch, "E48.34.0.3", {"start": v(28.45, 10.7) * mm, "end": v(28.1, 10.7) * mm});
            skLineSegment(sketch, "E48.direction1", {"start": v(-6.1, -3.17) * mm, "end": v(-5.08, -3.17) * mm, "construction": true});
            skSolve(sketch);
        }
        {
            var Q0;
            Q0=makeQuery(id+"F36.imprint","IMPRINT",FACE,{"disambiguationData":[TD([[makeQuery(id+"F36.imprint","IMPRINT",EDGE,{"derivedFrom":sQuery(id+"F36.wireOp",EDGE,"E44")}),-1.0]])]});
            var Q1;
            Q1=makeQuery(id+"F36.imprint","IMPRINT",FACE,{"disambiguationData":[TD([[makeQuery(id+"F36.imprint","IMPRINT",EDGE,{"derivedFrom":sQuery(id+"F36.wireOp",EDGE,"E48.1.0.0")}),1.0]])]});
            var Q2;
            Q2=makeQuery(id+"F36.imprint","IMPRINT",FACE,{"disambiguationData":[TD([[makeQuery(id+"F36.imprint","IMPRINT",EDGE,{"derivedFrom":sQuery(id+"F36.wireOp",EDGE,"E48.2.0.0")}),1.0]])]});
            var Q3;
            Q3=makeQuery(id+"F36.imprint","IMPRINT",FACE,{"disambiguationData":[TD([[makeQuery(id+"F36.imprint","IMPRINT",EDGE,{"derivedFrom":sQuery(id+"F36.wireOp",EDGE,"E48.3.0.0")}),1.0]])]});
            var Q4;
            Q4=makeQuery(id+"F36.imprint","IMPRINT",FACE,{"disambiguationData":[TD([[makeQuery(id+"F36.imprint","IMPRINT",EDGE,{"derivedFrom":sQuery(id+"F36.wireOp",EDGE,"E48.4.0.0")}),1.0]])]});
            var Q5;
            Q5=makeQuery(id+"F36.imprint","IMPRINT",FACE,{"disambiguationData":[TD([[makeQuery(id+"F36.imprint","IMPRINT",EDGE,{"derivedFrom":sQuery(id+"F36.wireOp",EDGE,"E48.5.0.0")}),1.0]])]});
            var Q6;
            Q6=makeQuery(id+"F36.imprint","IMPRINT",FACE,{"disambiguationData":[TD([[makeQuery(id+"F36.imprint","IMPRINT",EDGE,{"derivedFrom":sQuery(id+"F36.wireOp",EDGE,"E48.6.0.0")}),1.0]])]});
            var Q7;
            Q7=makeQuery(id+"F36.imprint","IMPRINT",FACE,{"disambiguationData":[TD([[makeQuery(id+"F36.imprint","IMPRINT",EDGE,{"derivedFrom":sQuery(id+"F36.wireOp",EDGE,"E48.7.0.0")}),1.0]])]});
            var Q8;
            Q8=makeQuery(id+"F36.imprint","IMPRINT",FACE,{"disambiguationData":[TD([[makeQuery(id+"F36.imprint","IMPRINT",EDGE,{"derivedFrom":sQuery(id+"F36.wireOp",EDGE,"E48.8.0.0")}),1.0]])]});
            var Q9;
            Q9=makeQuery(id+"F36.imprint","IMPRINT",FACE,{"disambiguationData":[TD([[makeQuery(id+"F36.imprint","IMPRINT",EDGE,{"derivedFrom":sQuery(id+"F36.wireOp",EDGE,"E48.9.0.0")}),1.0]])]});
            var Q10;
            Q10=makeQuery(id+"F36.imprint","IMPRINT",FACE,{"disambiguationData":[TD([[makeQuery(id+"F36.imprint","IMPRINT",EDGE,{"derivedFrom":sQuery(id+"F36.wireOp",EDGE,"E48.10.0.0")}),1.0]])]});
            var Q11;
            Q11=makeQuery(id+"F36.imprint","IMPRINT",FACE,{"disambiguationData":[TD([[makeQuery(id+"F36.imprint","IMPRINT",EDGE,{"derivedFrom":sQuery(id+"F36.wireOp",EDGE,"E48.11.0.0")}),1.0]])]});
            var Q12;
            Q12=makeQuery(id+"F36.imprint","IMPRINT",FACE,{"disambiguationData":[TD([[makeQuery(id+"F36.imprint","IMPRINT",EDGE,{"derivedFrom":sQuery(id+"F36.wireOp",EDGE,"E48.12.0.0")}),1.0]])]});
            var Q13;
            Q13=makeQuery(id+"F36.imprint","IMPRINT",FACE,{"disambiguationData":[TD([[makeQuery(id+"F36.imprint","IMPRINT",EDGE,{"derivedFrom":sQuery(id+"F36.wireOp",EDGE,"E48.13.0.0")}),1.0]])]});
            var Q14;
            Q14=makeQuery(id+"F36.imprint","IMPRINT",FACE,{"disambiguationData":[TD([[makeQuery(id+"F36.imprint","IMPRINT",EDGE,{"derivedFrom":sQuery(id+"F36.wireOp",EDGE,"E48.14.0.0")}),1.0]])]});
            var Q15;
            Q15=makeQuery(id+"F36.imprint","IMPRINT",FACE,{"disambiguationData":[TD([[makeQuery(id+"F36.imprint","IMPRINT",EDGE,{"derivedFrom":sQuery(id+"F36.wireOp",EDGE,"E48.15.0.0")}),1.0]])]});
            var Q16;
            Q16=makeQuery(id+"F36.imprint","IMPRINT",FACE,{"disambiguationData":[TD([[makeQuery(id+"F36.imprint","IMPRINT",EDGE,{"derivedFrom":sQuery(id+"F36.wireOp",EDGE,"E48.16.0.0")}),1.0]])]});
            var Q17;
            Q17=makeQuery(id+"F36.imprint","IMPRINT",FACE,{"disambiguationData":[TD([[makeQuery(id+"F36.imprint","IMPRINT",EDGE,{"derivedFrom":sQuery(id+"F36.wireOp",EDGE,"E48.17.0.0")}),1.0]])]});
            var Q18;
            Q18=makeQuery(id+"F36.imprint","IMPRINT",FACE,{"disambiguationData":[TD([[makeQuery(id+"F36.imprint","IMPRINT",EDGE,{"derivedFrom":sQuery(id+"F36.wireOp",EDGE,"E48.18.0.0")}),1.0]])]});
            var Q19;
            Q19=makeQuery(id+"F36.imprint","IMPRINT",FACE,{"disambiguationData":[TD([[makeQuery(id+"F36.imprint","IMPRINT",EDGE,{"derivedFrom":sQuery(id+"F36.wireOp",EDGE,"E48.19.0.0")}),1.0]])]});
            var Q20;
            Q20=makeQuery(id+"F36.imprint","IMPRINT",FACE,{"disambiguationData":[TD([[makeQuery(id+"F36.imprint","IMPRINT",EDGE,{"derivedFrom":sQuery(id+"F36.wireOp",EDGE,"E48.20.0.0")}),1.0]])]});
            var Q21;
            Q21=makeQuery(id+"F36.imprint","IMPRINT",FACE,{"disambiguationData":[TD([[makeQuery(id+"F36.imprint","IMPRINT",EDGE,{"derivedFrom":sQuery(id+"F36.wireOp",EDGE,"E48.21.0.0")}),1.0]])]});
            var Q22;
            Q22=makeQuery(id+"F36.imprint","IMPRINT",FACE,{"disambiguationData":[TD([[makeQuery(id+"F36.imprint","IMPRINT",EDGE,{"derivedFrom":sQuery(id+"F36.wireOp",EDGE,"E48.22.0.0")}),1.0]])]});
            var Q23;
            Q23=makeQuery(id+"F36.imprint","IMPRINT",FACE,{"disambiguationData":[TD([[makeQuery(id+"F36.imprint","IMPRINT",EDGE,{"derivedFrom":sQuery(id+"F36.wireOp",EDGE,"E48.23.0.0")}),1.0]])]});
            var Q24;
            Q24=makeQuery(id+"F36.imprint","IMPRINT",FACE,{"disambiguationData":[TD([[makeQuery(id+"F36.imprint","IMPRINT",EDGE,{"derivedFrom":sQuery(id+"F36.wireOp",EDGE,"E48.24.0.0")}),1.0]])]});
            var Q25;
            Q25=makeQuery(id+"F36.imprint","IMPRINT",FACE,{"disambiguationData":[TD([[makeQuery(id+"F36.imprint","IMPRINT",EDGE,{"derivedFrom":sQuery(id+"F36.wireOp",EDGE,"E48.25.0.0")}),1.0]])]});
            var Q26;
            Q26=makeQuery(id+"F36.imprint","IMPRINT",FACE,{"disambiguationData":[TD([[makeQuery(id+"F36.imprint","IMPRINT",EDGE,{"derivedFrom":sQuery(id+"F36.wireOp",EDGE,"E48.26.0.0")}),1.0]])]});
            var Q27;
            Q27=makeQuery(id+"F36.imprint","IMPRINT",FACE,{"disambiguationData":[TD([[makeQuery(id+"F36.imprint","IMPRINT",EDGE,{"derivedFrom":sQuery(id+"F36.wireOp",EDGE,"E48.27.0.0")}),1.0]])]});
            var Q28;
            Q28=makeQuery(id+"F36.imprint","IMPRINT",FACE,{"disambiguationData":[TD([[makeQuery(id+"F36.imprint","IMPRINT",EDGE,{"derivedFrom":sQuery(id+"F36.wireOp",EDGE,"E48.28.0.0")}),1.0]])]});
            var Q29;
            Q29=makeQuery(id+"F36.imprint","IMPRINT",FACE,{"disambiguationData":[TD([[makeQuery(id+"F36.imprint","IMPRINT",EDGE,{"derivedFrom":sQuery(id+"F36.wireOp",EDGE,"E48.29.0.0")}),1.0]])]});
            var Q30;
            Q30=makeQuery(id+"F36.imprint","IMPRINT",FACE,{"disambiguationData":[TD([[makeQuery(id+"F36.imprint","IMPRINT",EDGE,{"derivedFrom":sQuery(id+"F36.wireOp",EDGE,"E48.30.0.0")}),1.0]])]});
            var Q31;
            Q31=makeQuery(id+"F36.imprint","IMPRINT",FACE,{"disambiguationData":[TD([[makeQuery(id+"F36.imprint","IMPRINT",EDGE,{"derivedFrom":sQuery(id+"F36.wireOp",EDGE,"E48.31.0.0")}),1.0]])]});
            var Q32;
            Q32=makeQuery(id+"F36.imprint","IMPRINT",FACE,{"disambiguationData":[TD([[makeQuery(id+"F36.imprint","IMPRINT",EDGE,{"derivedFrom":sQuery(id+"F36.wireOp",EDGE,"E48.32.0.0")}),1.0]])]});
            var Q33;
            Q33=makeQuery(id+"F36.imprint","IMPRINT",FACE,{"disambiguationData":[TD([[makeQuery(id+"F36.imprint","IMPRINT",EDGE,{"derivedFrom":sQuery(id+"F36.wireOp",EDGE,"E48.33.0.0")}),1.0]])]});
            var Q34;
            Q34=makeQuery(id+"F36.imprint","IMPRINT",FACE,{"disambiguationData":[TD([[makeQuery(id+"F36.imprint","IMPRINT",EDGE,{"derivedFrom":sQuery(id+"F36.wireOp",EDGE,"E48.34.0.0")}),1.0]])]});
            extrude(context, id + "F37", {"entities" : qUnion([Q0, Q1, Q2, Q3, Q4, Q5, Q6, Q7, Q8, Q9, Q10, Q11, Q12, Q13, Q14, Q15, Q16, Q17, Q18, Q19, Q20, Q21, Q22, Q23, Q24, Q25, Q26, Q27, Q28, Q29, Q30, Q31, Q32, Q33, Q34]), "operationType" : NewBodyOperationType.REMOVE, "oppositeDirection" : true, "depth" : 2.54 * mm, "offsetDistance" : 25.4 * mm});
        }
    });
